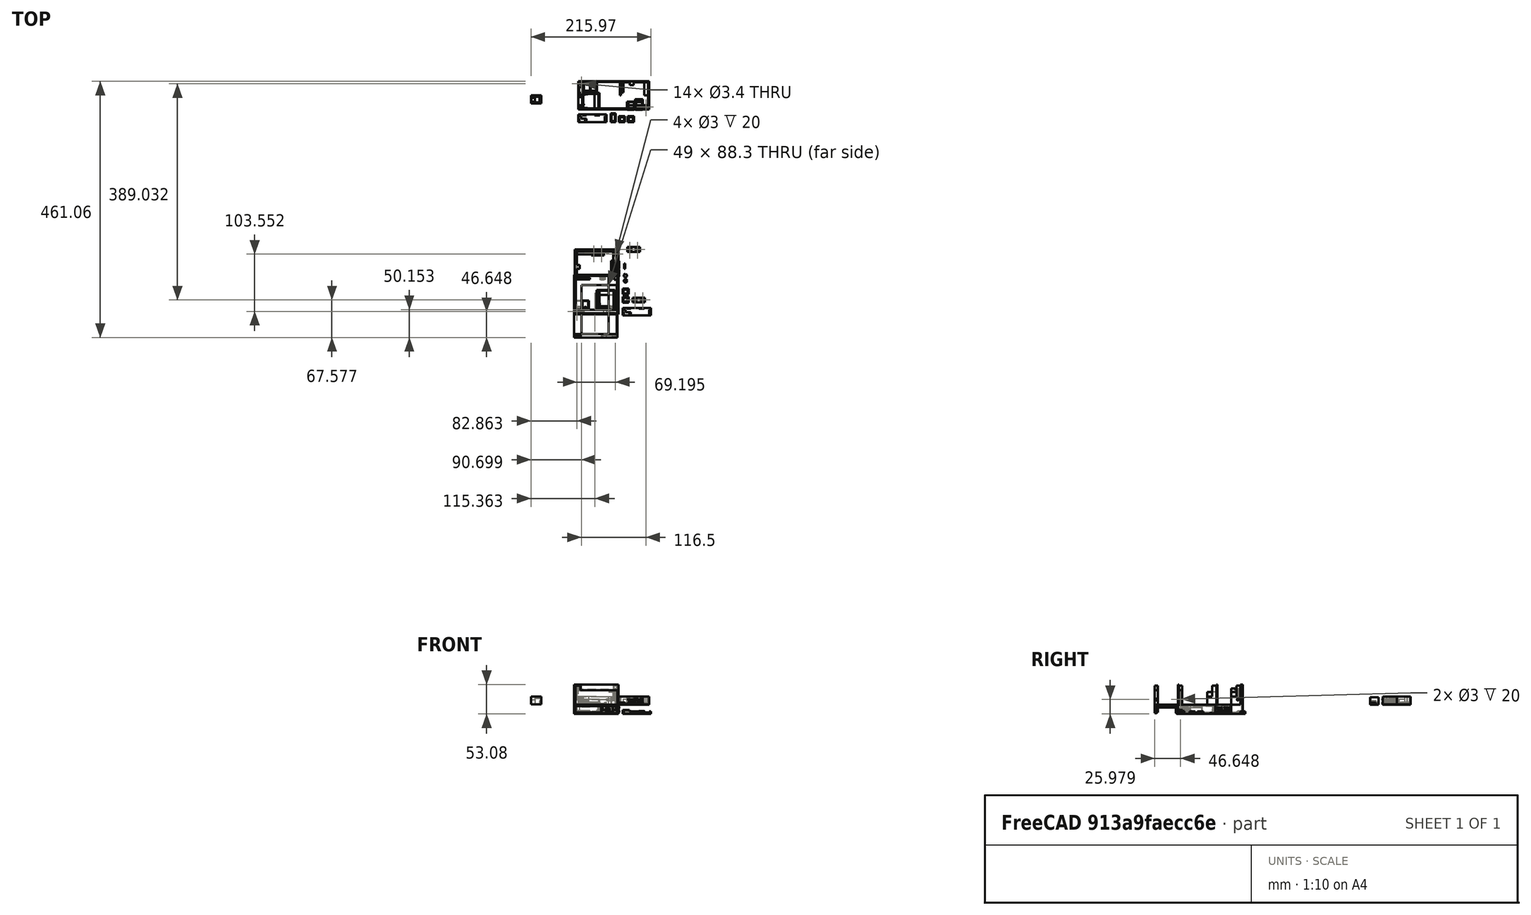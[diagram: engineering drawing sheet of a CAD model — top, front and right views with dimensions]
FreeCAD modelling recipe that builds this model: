
FCSTD DOCUMENT  (FreeCAD 0.18.4R)
Label: control.station.lamp.pump
License: All rights reserved
LicenseURL: http://en.wikipedia.org/wiki/All_rights_reserved
objects: Part::Extrusion×146, Part::Feature×99, Part::Part2DObjectPython×90, Part::MultiFuse×70, Part::Cut×57, Part::FeaturePython×25, App::DocumentObjectGroup×12, Part::Cone×5
note: 492 computed .brp shape members not serialized (recipe doc carries the construction recipe); baked Part::Feature solids carry a one-line shape summary decoded from their .brp

FEATURE [Part::Feature] Cut005001  label="Cut006"
  Placement = pos=(-97.5132,168.752,-89.7646) rot=(0,-1,0;1.57274rad)
  shape: bbox 38.06 x 11.04 x 29.87 mm, 51 faces (baked)
FEATURE [Part::Part2DObjectPython] Rectangle004  # Draft 2D object (typed FeaturePython)
  ChamferSize = 0
  Columns = 1
  FilletRadius = 0
  Height = 76.4161
  Length = 78.2176
  MakeFace = true
  Placement = pos=(-30.7742,-1.04013,-53.231) rot=(1,0,0;1.5708rad)
  Rows = 1
  Support = -> [Cut005001]
FEATURE [Part::Extrusion] Extrusion008
  Base = -> Rectangle004
  Dir = (-5.996e-12,1.04013,2.61633e-11)
  DirMode = 0
  FaceMakerClass = Part::FaceMakerBullseye
  LengthFwd = 0
  LengthRev = 0
  Solid = true
  Symmetric = false
FEATURE [Part::Cut] Cut005002
  Base = -> Cut005001
  Tool = -> Extrusion008
FEATURE [Part::Feature] Face004
  shape: bbox 0.05017 x 0.9599 x 25.8 mm, 1 faces, 0 solids (baked)
FEATURE [Part::Extrusion] Extrusion009
  Base = -> Face004
  Dir = (5.49999,-2.0138e-11,0.0106907)
  DirMode = 0
  FaceMakerClass = Part::FaceMakerBullseye
  LengthFwd = 0
  LengthRev = 0
  Solid = true
  Symmetric = false
FEATURE [Part::Cut] Cut005003
  Base = -> Cut005002
  Placement = pos=(-16.5699,14.4997,-128.121) rot=(0,1,0;0.001944rad)
  Tool = -> Extrusion009
FEATURE [Part::Feature] Face
  Placement = pos=(-35.171,9.5,-126.101) rot=(0,0,1;0rad)
  shape: bbox 15.9 x 4e-07 x 10.7 mm, 1 faces, 0 solids (baked)
FEATURE [Part::Extrusion] Extrusion016
  Base = -> Face
  Dir = (0,-1.5,0)
  DirMode = 0
  FaceMakerClass = Part::FaceMakerBullseye
  LengthFwd = 0
  LengthRev = 0
  Placement = pos=(108.58,10.9997,-148.572) rot=(0,1,0;1.5708rad)
  Solid = true
  Symmetric = false
FEATURE [Part::Feature] Face005
  Placement = pos=(-35.171,9.5,-126.101) rot=(0,0,1;0rad)
  shape: bbox 15.9 x 4e-07 x 10.7 mm, 1 faces, 0 solids (baked)
FEATURE [Part::Extrusion] Extrusion017
  Base = -> Face005
  Dir = (0,-1.5,0)
  DirMode = 0
  FaceMakerClass = Part::FaceMakerBullseye
  LengthFwd = 0
  LengthRev = 0
  Placement = pos=(-8.2,-99.2512,-120.601) rot=(1,0,0;1.5708rad)
  Solid = true
  Symmetric = false
FEATURE [Part::Feature] Fusion001002003002001  label="Fusion001002003003"
  shape: bbox 18.6 x 15 x 50.4 mm, 8 faces (baked)
FEATURE [Part::Feature] Face013
  shape: bbox 18.6 x 15 x 6.403e-07 mm, 1 faces, 0 solids (baked)
FEATURE [Part::Extrusion] Extrusion026
  Base = -> Face013
  Dir = (0,1.05e-14,-25)
  DirMode = 0
  FaceMakerClass = Part::FaceMakerBullseye
  LengthFwd = 0
  LengthRev = 0
  Solid = true
  Symmetric = false
FEATURE [Part::Cut] Cut279012005005004
  Base = -> Fusion001002003002001
  Tool = -> Extrusion026
FEATURE [Part::Part2DObjectPython] Rectangle012  # Draft 2D object (typed FeaturePython)
  ChamferSize = 0
  Columns = 1
  FilletRadius = 0
  Height = 50.4
  Length = 127.7
  MakeFace = true
  Placement = pos=(-45.471,23.4997,-158.501) rot=(1,0,0;1.5708rad)
  Rows = 1
  Support = -> [Cut005003]
FEATURE [Part::Extrusion] Extrusion028
  Base = -> Rectangle012
  Dir = (-2.8e-15,1,-1.17319e-11)
  DirMode = 0
  FaceMakerClass = Part::FaceMakerBullseye
  LengthFwd = 0
  LengthRev = 0
  Solid = true
  Symmetric = false
FEATURE [Part::Part2DObjectPython] Circle005  # Draft 2D object (typed FeaturePython)
  FirstAngle = 0
  LastAngle = 0
  MakeFace = true
  Placement = pos=(-39.871,9.5,-112.551) rot=(1,0,0;1.5708rad)
  Radius = 1.7
FEATURE [Part::Extrusion] Extrusion029
  Base = -> Circle005
  Dir = (1.7e-15,43.004,9.5e-15)
  DirMode = 0
  FaceMakerClass = Part::FaceMakerBullseye
  LengthFwd = 0
  LengthRev = 0
  Solid = true
  Symmetric = false
FEATURE [Part::Cut] Cut279012005005005
  Base = -> Extrusion028
  Tool = -> Extrusion029
FEATURE [Part::Part2DObjectPython] Circle006  # Draft 2D object (typed FeaturePython)
  FirstAngle = 0
  LastAngle = 0
  MakeFace = true
  Placement = pos=(76.629,9.5,-154.051) rot=(1,0,0;1.5708rad)
  Radius = 1.7
  Support = -> [Cut279012005005004]
FEATURE [Part::Extrusion] Extrusion030
  Base = -> Circle006
  Dir = (1e-15,47.7104,-1.06e-14)
  DirMode = 0
  FaceMakerClass = Part::FaceMakerBullseye
  LengthFwd = 0
  LengthRev = 0
  Solid = true
  Symmetric = false
FEATURE [Part::Cut] Cut279012005005006
  Base = -> Cut279012005005005
  Tool = -> Extrusion030
FEATURE [Part::Part2DObjectPython] Rectangle013  # Draft 2D object (typed FeaturePython)
  ChamferSize = 0
  Columns = 1
  FilletRadius = 0
  Height = 10.4
  Length = 8.1
  MakeFace = true
  Placement = pos=(-38.471,9.5,-130.801) rot=(1,0,0;1.5708rad)
  Rows = 1
FEATURE [Part::Part2DObjectPython] Rectangle014  # Draft 2D object (typed FeaturePython)
  ChamferSize = 0
  Columns = 1
  FilletRadius = 0
  Height = 10.4
  Length = 8.1
  MakeFace = true
  Placement = pos=(-38.471,9.5,-146.201) rot=(1,0,0;1.5708rad)
  Rows = 1
FEATURE [Part::Extrusion] Extrusion031
  Base = -> Rectangle013
  Dir = (3.6e-15,89.6542,1.99e-14)
  DirMode = 0
  FaceMakerClass = Part::FaceMakerBullseye
  LengthFwd = 0
  LengthRev = 0
  Solid = true
  Symmetric = false
FEATURE [Part::Extrusion] Extrusion032
  Base = -> Rectangle014
  Dir = (3.5e-15,84.9482,1.89e-14)
  DirMode = 0
  FaceMakerClass = Part::FaceMakerBullseye
  LengthFwd = 0
  LengthRev = 0
  Solid = true
  Symmetric = false
FEATURE [Part::Cut] Cut279012005005007
  Base = -> Cut279012005005006
  Tool = -> Extrusion032
FEATURE [Part::Cut] Cut279012005005008
  Base = -> Cut279012005005007
  Tool = -> Extrusion031
FEATURE [Part::Part2DObjectPython] Rectangle015  # Draft 2D object (typed FeaturePython)
  ChamferSize = 0
  Columns = 1
  FilletRadius = 0
  Height = 9.3
  Length = 17.1
  MakeFace = true
  Placement = pos=(-43.971,9.5,-157.001) rot=(1,0,0;1.5708rad)
  Rows = 1
FEATURE [Part::Feature] Fusion001002003002002001  label="Fusion001002003002003"
  shape: bbox 18.6 x 15 x 50.4 mm, 38 faces (baked)
FEATURE [Part::Extrusion] Extrusion033
  Base = -> Rectangle015
  Dir = (5e-16,45.0707,-1e-14)
  DirMode = 0
  FaceMakerClass = Part::FaceMakerBullseye
  LengthFwd = 0
  LengthRev = 0
  Solid = true
  Symmetric = false
FEATURE [Part::Cut] Cut279012005005009
  Base = -> Fusion001002003002002001
  Tool = -> Extrusion033
FEATURE [Part::Part2DObjectPython] Rectangle016  # Draft 2D object (typed FeaturePython)
  ChamferSize = 0
  Columns = 1
  FilletRadius = 0
  Height = 9.3
  Length = 17.1
  MakeFace = true
  Placement = pos=(-43.971,9.5,-157.001) rot=(1,0,0;1.5708rad)
  Rows = 1
  Support = -> [Cut279012005005009]
FEATURE [Part::Extrusion] Extrusion034
  Base = -> Rectangle016
  Dir = (1.8e-15,174.192,-3.87e-14)
  DirMode = 0
  FaceMakerClass = Part::FaceMakerBullseye
  LengthFwd = 0
  LengthRev = 0
  Solid = true
  Symmetric = false
FEATURE [Part::Cut] Cut279012005005010
  Base = -> Cut279012005005008
  Tool = -> Extrusion034
FEATURE [Part::Part2DObjectPython] Rectangle017  # Draft 2D object (typed FeaturePython)
  ChamferSize = 0
  Columns = 1
  FilletRadius = 0
  Height = 25.2
  Length = 9.3
  MakeFace = true
  Placement = pos=(72.929,23.4997,-133.301) rot=(1,0,0;1.5708rad)
  Rows = 1
  Support = -> [Cut279012005005010]
FEATURE [Part::Extrusion] Extrusion035
  Base = -> Rectangle017
  Dir = (-2.63e-14,9.53056,-1.11812e-10)
  DirMode = 0
  FaceMakerClass = Part::FaceMakerBullseye
  LengthFwd = 0
  LengthRev = 0
  Solid = true
  Symmetric = false
FEATURE [Part::Cut] Cut279012005005011
  Base = -> Cut279012005005010
  Tool = -> Extrusion035
FEATURE [Part::Part2DObjectPython] Rectangle018  # Draft 2D object (typed FeaturePython)
  ChamferSize = 0
  Columns = 1
  FilletRadius = 0
  Height = 16.25
  Length = 17.1
  MakeFace = true
  Placement = pos=(63.629,9.5,-150.851) rot=(1,0,0;1.5708rad)
  Rows = 1
FEATURE [Part::Extrusion] Extrusion036
  Base = -> Rectangle018
  Dir = (3e-16,13.9997,-3.1e-15)
  DirMode = 0
  FaceMakerClass = Part::FaceMakerBullseye
  LengthFwd = 0
  LengthRev = 0
  Solid = true
  Symmetric = false
FEATURE [Part::Cut] Cut279012005005012
  Base = -> Cut279012005005004
  Tool = -> Extrusion036
FEATURE [Part::Feature] Face015
  shape: bbox 6.403e-07 x 15 x 25.4 mm, 1 faces, 0 solids (baked)
FEATURE [Part::Extrusion] Extrusion037
  Base = -> Face015
  Dir = (7.3,0,-2.1e-15)
  DirMode = 0
  FaceMakerClass = Part::FaceMakerBullseye
  LengthFwd = 0
  LengthRev = 0
  Solid = true
  Symmetric = false
FEATURE [Part::Cut] Cut279012005005013
  Base = -> Cut279012005005012
  Tool = -> Extrusion037
FEATURE [Part::Feature] Fusion001002003002002003001  label="Fusion001002003002002004"
  shape: bbox 53 x 16 x 25 mm, 32 faces (baked)
FEATURE [Part::Feature] Fusion001002003002002003002  label="Fusion001002003002002005"
  shape: bbox 53 x 16 x 25 mm, 32 faces (baked)
FEATURE [Part::Part2DObjectPython] Rectangle019  # Draft 2D object (typed FeaturePython)
  ChamferSize = 0
  Columns = 1
  FilletRadius = 0
  Height = 9.44975
  Length = 9.8
  MakeFace = true
  Placement = pos=(-36.671,9.5,-118.901) rot=(1,0,0;1.5708rad)
  Rows = 1
FEATURE [Part::Extrusion] Extrusion039
  Base = -> Rectangle019
  Dir = (6e-16,13.9997,3.1e-15)
  DirMode = 0
  FaceMakerClass = Part::FaceMakerBullseye
  LengthFwd = 0
  LengthRev = 0
  Solid = true
  Symmetric = false
FEATURE [Part::Cut] Cut279012005005014
  Base = -> Cut279012005005009
  Tool = -> Extrusion039
FEATURE [Part::Part2DObjectPython] Rectangle020  # Draft 2D object (typed FeaturePython)
  ChamferSize = 0
  Columns = 1
  FilletRadius = 0
  Height = 2
  Length = 28.5
  MakeFace = true
  Placement = pos=(11.129,14.4997,-158.501) rot=(1,0,0;1.5708rad)
  Rows = 1
FEATURE [Part::Extrusion] Extrusion040
  Base = -> Rectangle020
  Dir = (-5.12376e-11,9,2.26487e-10)
  DirMode = 0
  FaceMakerClass = Part::FaceMakerBullseye
  LengthFwd = 0
  LengthRev = 0
  Solid = true
  Symmetric = false
FEATURE [Part::MultiFuse] Fusion001002003002002003003
  Shapes = -> [Cut279012005005011,Cut279012005005014,Cut005003,Fusion001002003002002003001,Extrusion040]
FEATURE [Part::Part2DObjectPython] Rectangle021  # Draft 2D object (typed FeaturePython)
  ChamferSize = 0
  Columns = 1
  FilletRadius = 0
  Height = 11.7
  Length = 16.9
  MakeFace = true
  Placement = pos=(-39.0339,9.5,-104.973) rot=(1,0,0;1.5708rad)
  Rows = 1
FEATURE [Part::Extrusion] Extrusion041
  Base = -> Rectangle021
  Dir = (-1e-16,-3,7e-16)
  DirMode = 0
  FaceMakerClass = Part::FaceMakerBullseye
  LengthFwd = 0
  LengthRev = 0
  Placement = pos=(-108.444,29.9997,-147.135) rot=(0.707107,0,-0.707107;3.14159rad)
  Solid = true
  Symmetric = false
FEATURE [Part::Part2DObjectPython] Circle007  # Draft 2D object (typed FeaturePython)
  FirstAngle = 0
  LastAngle = 0
  MakeFace = true
  Placement = pos=(-18.371,24.4997,-149.501) rot=(-1,0,0;1.5708rad)
  Radius = 1.5
  Support = -> [Fusion001002003002002003003]
FEATURE [Part::Extrusion] Extrusion042
  Base = -> Circle007
  Dir = (6.94e-14,-25.137,2.94906e-10)
  DirMode = 0
  FaceMakerClass = Part::FaceMakerBullseye
  LengthFwd = 0
  LengthRev = 0
  Solid = true
  Symmetric = false
FEATURE [Part::Cut] Cut279012005005015
  Base = -> Fusion001002003002002003003
  Tool = -> Extrusion042
FEATURE [Part::Extrusion] Extrusion043
  Base = -> Rectangle021
  Dir = (-1e-16,-3,7e-16)
  DirMode = 0
  FaceMakerClass = Part::FaceMakerBullseye
  LengthFwd = 0
  LengthRev = 0
  Placement = pos=(42.0628,116.773,-101.601) rot=(-1,0,0;1.5708rad)
  Solid = true
  Symmetric = false
FEATURE [Part::MultiFuse] Fusion001002003002002003004
  Shapes = -> [Cut279012005005015,Fusion001002003002002003002,Cut279012005005013]
FEATURE [Part::Cut] Cut279012005005016
  Base = -> Extrusion043
  Placement = pos=(-15.2708,131.601,-111.13) rot=(-0.57735,-0.57735,-0.57735;2.0944rad)
  Tool = -> Extrusion017
FEATURE [Part::Part2DObjectPython] Rectangle022  # Draft 2D object (typed FeaturePython)
  ChamferSize = 0
  Columns = 1
  FilletRadius = 0
  Height = 1
  Length = 11.7
  MakeFace = true
  Placement = pos=(8.22896,23.4997,-91.2009) rot=(0,0.707107,0.707107;3.14159rad)
  Rows = 1
FEATURE [Part::Extrusion] Extrusion044
  Base = -> Rectangle022
  Dir = (0,-3,-4e-15)
  DirMode = 0
  FaceMakerClass = Part::FaceMakerBullseye
  LengthFwd = 0
  LengthRev = 0
  Solid = true
  Symmetric = false
FEATURE [Part::MultiFuse] Fusion001002003002002003005
  Placement = pos=(-23.4,1.322e-12,-17.9) rot=(0,0,1;0rad)
  Shapes = -> [Cut279012005005016,Extrusion044]
FEATURE [Part::Feature] Face017
  Placement = pos=(-108.444,29.9997,-147.135) rot=(0.707107,0,-0.707107;3.14159rad)
  shape: bbox 11.7 x 3 x 2e-07 mm, 1 faces, 0 solids (baked)
FEATURE [Part::Extrusion] Extrusion045
  Base = -> Face017
  Dir = (-3e-16,-3e-16,-1)
  DirMode = 0
  FaceMakerClass = Part::FaceMakerBullseye
  LengthFwd = 0
  LengthRev = 0
  Solid = true
  Symmetric = false
FEATURE [Part::MultiFuse] Fusion001002003002002003006
  Shapes = -> [Extrusion041,Extrusion045]
FEATURE [Part::Feature] Face018
  shape: bbox 2e-07 x 3 x 16.9 mm, 1 faces, 0 solids (baked)
FEATURE [Part::Extrusion] Extrusion046
  Base = -> Face018
  Dir = (1,0,-3e-16)
  DirMode = 0
  FaceMakerClass = Part::FaceMakerBullseye
  LengthFwd = 0
  LengthRev = 0
  Solid = true
  Symmetric = false
FEATURE [Part::Cut] Cut279012005005017
  Base = -> Fusion001002003002002003006
  Tool = -> Extrusion016
FEATURE [Part::Feature] Face019
  shape: bbox 1 x 3 x 2e-07 mm, 1 faces, 0 solids (baked)
FEATURE [Part::Extrusion] Extrusion047
  Base = -> Face019
  Dir = (-3e-16,-3e-16,-1)
  DirMode = 0
  FaceMakerClass = Part::FaceMakerBullseye
  LengthFwd = 0
  LengthRev = 0
  Solid = true
  Symmetric = false
FEATURE [Part::MultiFuse] Fusion001002003002002003007
  Shapes = -> [Extrusion046,Extrusion047,Cut279012005005017]
FEATURE [Part::Part2DObjectPython] Circle008  # Draft 2D object (typed FeaturePython)
  FirstAngle = 0
  LastAngle = 0
  MakeFace = true
  Placement = pos=(-8.82104,20.4997,-112.101) rot=(1,0,0;1.5708rad)
  Radius = 2
  Support = -> [Fusion001002003002002003007]
FEATURE [Part::Part2DObjectPython] Circle009  # Draft 2D object (typed FeaturePython)
  FirstAngle = 0
  LastAngle = 0
  MakeFace = true
  Placement = pos=(-20.521,20.4997,-112.101) rot=(1,0,0;1.5708rad)
  Radius = 2.2
FEATURE [Part::Extrusion] Extrusion048
  Base = -> Circle008
  Dir = (-3e-16,18.8724,-8.4e-15)
  DirMode = 0
  FaceMakerClass = Part::FaceMakerBullseye
  LengthFwd = 0
  LengthRev = 0
  Solid = true
  Symmetric = false
FEATURE [Part::Extrusion] Extrusion049
  Base = -> Circle009
  Dir = (5e-16,17.7937,2.37e-14)
  DirMode = 0
  FaceMakerClass = Part::FaceMakerBullseye
  LengthFwd = 0
  LengthRev = 0
  Solid = true
  Symmetric = false
FEATURE [Part::MultiFuse] Fusion001002003002002003008
  Shapes = -> [Fusion001002003002002003004,Fusion001002003002002003007,Fusion001002003002002003005]
FEATURE [Part::Cut] Cut279012005005018
  Base = -> Fusion001002003002002003008
  Tool = -> Extrusion048
FEATURE [Part::Cut] Cut279012005005019
  Base = -> Cut279012005005018
  Tool = -> Extrusion049
FEATURE [Part::Part2DObjectPython] Rectangle023  # Draft 2D object (typed FeaturePython)
  ChamferSize = 0
  Columns = 1
  FilletRadius = 0
  Height = 83.9051
  Length = 94.4421
  MakeFace = true
  Placement = pos=(-5.29718,24.4997,-89.2462) rot=(-1,0,0;1.5708rad)
  Rows = 1
  Support = -> [Cut279012005005019]
FEATURE [Part::Extrusion] Extrusion050
  Base = -> Rectangle023
  Dir = (-2.099e-13,76.0573,-8.92301e-10)
  DirMode = 0
  FaceMakerClass = Part::FaceMakerBullseye
  LengthFwd = 0
  LengthRev = 0
  Solid = true
  Symmetric = false
FEATURE [Part::Cut] Cut279012005005020
  Base = -> Cut279012005005019
  Placement = pos=(0,183.001,-134.001) rot=(-1,0,0;1.5708rad)
  Tool = -> Extrusion050
FEATURE [Part::Part2DObjectPython] Rectangle024  # Draft 2D object (typed FeaturePython)
  ChamferSize = 0
  Columns = 1
  FilletRadius = 0
  Height = 108.906
  Length = 167.513
  MakeFace = true
  Placement = pos=(-67.949,-9.40096,-157.501) rot=(0,0,1;0rad)
  Rows = 1
  Support = -> [Cut279012005005020]
FEATURE [Part::FeaturePython] Slice  # WARN: FeaturePython — macro-defined, semantics opaque (R4)
  Base = -> Cut279012005005020
  Mode = 1
  Tolerance = 0
  Tools = -> [Rectangle024]
FEATURE [Part::FeaturePython] Slice_child0  label="Slice.0"  # WARN: FeaturePython — macro-defined, semantics opaque (R4)
  Base = -> Slice
  FilterType = 1
  Invert = false
  OverrideMaxVal = 0
  WindowFrom = 80
  WindowTo = 100
  items = 0
FEATURE [Part::FeaturePython] Slice_child1  label="Slice.1"  # WARN: FeaturePython — macro-defined, semantics opaque (R4)
  Base = -> Slice
  FilterType = 1
  Invert = false
  OverrideMaxVal = 0
  WindowFrom = 80
  WindowTo = 100
  items = 1
FEATURE [Part::FeaturePython] Slice_child2  label="Slice.2"  # WARN: FeaturePython — macro-defined, semantics opaque (R4)
  Base = -> Slice
  FilterType = 1
  Invert = false
  OverrideMaxVal = 0
  WindowFrom = 80
  WindowTo = 100
  items = 2
FEATURE [Part::Part2DObjectPython] Rectangle025  # Draft 2D object (typed FeaturePython)
  ChamferSize = 0
  Columns = 1
  FilletRadius = 0
  Height = 53.366
  Length = 63.9307
  MakeFace = true
  Placement = pos=(-26.871,20.4259,-172.171) rot=(0.57735,0.57735,0.57735;2.0944rad)
  Rows = 1
  Support = -> [Slice_child0]
FEATURE [Part::FeaturePython] Slice001  # WARN: FeaturePython — macro-defined, semantics opaque (R4)
  Base = -> Slice_child0
  Mode = 1
  Tolerance = 0
  Tools = -> [Rectangle025]
FEATURE [Part::FeaturePython] Slice001_child0  label="Slice001.0"  # WARN: FeaturePython — macro-defined, semantics opaque (R4)
  Base = -> Slice001
  FilterType = 1
  Invert = false
  OverrideMaxVal = 0
  Placement = pos=(-18.6,-1.1717e-11,5.18099e-10) rot=(0,0,1;0rad)
  WindowFrom = 80
  WindowTo = 100
  items = 0
FEATURE [Part::FeaturePython] Slice001_child2  label="Slice001.2"  # WARN: FeaturePython — macro-defined, semantics opaque (R4)
  Base = -> Slice001
  FilterType = 1
  Invert = false
  OverrideMaxVal = 0
  Placement = pos=(-9.3,8.5e-14,1.21162e-10) rot=(0,0,1;0rad)
  WindowFrom = 80
  WindowTo = 100
  items = 2
FEATURE [App::DocumentObjectGroup] GrExplode_Slice002  label="Exploded Slice002"
FEATURE [Part::FeaturePython] Slice003_child1  label="Slice003.1"  # WARN: FeaturePython — macro-defined, semantics opaque (R4)
  FilterType = 1
  Invert = false
  OverrideMaxVal = 0
  Placement = pos=(-85.1,-3.4521e-10,1.21162e-10) rot=(0,0,1;0rad)
  WindowFrom = 80
  WindowTo = 100
  items = 1
FEATURE [Part::Feature] Face020
  shape: bbox 7.019e-07 x 50.4 x 1 mm, 1 faces, 0 solids (baked)
FEATURE [Part::Extrusion] Extrusion051
  Base = -> Face020
  Dir = (85.1,2.6e-15,-2.375e-13)
  DirMode = 0
  FaceMakerClass = Part::FaceMakerBullseye
  LengthFwd = 0
  LengthRev = 0
  Solid = true
  Symmetric = false
FEATURE [Part::MultiFuse] Fusion001002003002002003009
  Shapes = -> [Slice_child1,Extrusion051]
FEATURE [Part::Part2DObjectPython] Rectangle028  # Draft 2D object (typed FeaturePython)
  ChamferSize = 0
  Columns = 1
  FilletRadius = 0
  Height = 152.897
  Length = 92.998
  MakeFace = true
  Placement = pos=(6.88981,49.8997,-45.1861) rot=(-1,0,0;1.5708rad)
  Rows = 1
FEATURE [Part::FeaturePython] Slice004  # WARN: FeaturePython — macro-defined, semantics opaque (R4)
  Base = -> Slice_child2
  Mode = 1
  Tolerance = 0
  Tools = -> [Rectangle028]
FEATURE [Part::FeaturePython] Slice004_child0  label="Slice004.0"  # WARN: FeaturePython — macro-defined, semantics opaque (R4)
  Base = -> Slice004
  FilterType = 1
  Invert = false
  OverrideMaxVal = 0
  Placement = pos=(9.3,-7e-15,-2.8e-14) rot=(0,0,1;0rad)
  WindowFrom = 80
  WindowTo = 100
  items = 0
FEATURE [Part::FeaturePython] Slice004_child1  label="Slice004.1"  # WARN: FeaturePython — macro-defined, semantics opaque (R4)
  Base = -> Slice004
  FilterType = 1
  Invert = false
  OverrideMaxVal = 0
  WindowFrom = 80
  WindowTo = 100
  items = 1
FEATURE [Part::Part2DObjectPython] Rectangle029  # Draft 2D object (typed FeaturePython)
  ChamferSize = 0
  Columns = 1
  FilletRadius = 0
  Height = 11.2
  Length = 10.6
  MakeFace = true
  Placement = pos=(-123.571,36.7997,-143.501) rot=(0,0,1;0rad)
  Rows = 1
FEATURE [Part::Extrusion] Extrusion052
  Base = -> Rectangle029
  Dir = (-1e-16,6e-16,-4)
  DirMode = 0
  FaceMakerClass = Part::FaceMakerBullseye
  LengthFwd = 0
  LengthRev = 0
  Solid = true
  Symmetric = false
FEATURE [Part::Cut] Cut279012005005021
  Base = -> Slice003_child1
  Tool = -> Extrusion052
FEATURE [Part::Feature] Face021
  Placement = pos=(-85.1,-3.4521e-10,1.21162e-10) rot=(0,0,1;0rad)
  shape: bbox 3.5 x 10.4 x 6.403e-07 mm, 1 faces, 0 solids (baked)
FEATURE [Part::Extrusion] Extrusion054
  Base = -> Face021
  Dir = (1e-16,3e-16,-1.4)
  DirMode = 0
  FaceMakerClass = Part::FaceMakerBullseye
  LengthFwd = 0
  LengthRev = 0
  Solid = true
  Symmetric = false
FEATURE [Part::Cut] Cut279012005005023
  Base = -> Cut279012005005021
  Tool = -> Extrusion054
FEATURE [Part::Feature] Face024
  shape: bbox 1 x 6.403e-07 x 1.4 mm, 1 faces, 0 solids (baked)
FEATURE [Part::Extrusion] Extrusion057
  Base = -> Face024
  Dir = (0,-8.4,-1.9e-15)
  DirMode = 0
  FaceMakerClass = Part::FaceMakerBullseye
  LengthFwd = 0
  LengthRev = 0
  Solid = true
  Symmetric = false
FEATURE [Part::MultiFuse] Fusion001002003002002003011
  Shapes = -> [Extrusion057,Cut279012005005023]
FEATURE [App::DocumentObjectGroup] GrExplode_Slice003  label="Exploded Slice003"
  Group = -> [Fusion001002003002002003011]
FEATURE [Part::Feature] Fusion001002003002002003011001  label="Fusion001002003002002003012"
  Placement = pos=(106.229,155.071,-5.99975) rot=(0,0,1;1.5708rad)
  shape: bbox 14.4 x 18.6 x 14 mm, 23 faces (baked)
FEATURE [Part::Part2DObjectPython] Circle010  # Draft 2D object (typed FeaturePython)
  FirstAngle = 0
  LastAngle = 0
  MakeFace = true
  Placement = pos=(-39.871,70.4497,-157.501) rot=(0,0,1;0rad)
  Radius = 1.7
  Support = -> [Fusion001002003002002003009]
FEATURE [Part::Extrusion] Extrusion060
  Base = -> Circle010
  Dir = (-1.949e-13,-8.19475e-10,-69.8512)
  DirMode = 0
  FaceMakerClass = Part::FaceMakerBullseye
  LengthFwd = 0
  LengthRev = 0
  Solid = true
  Symmetric = false
FEATURE [Part::Cut] Cut279012005005027
  Base = -> Fusion001002003002002003009
  Tool = -> Extrusion060
FEATURE [Part::FeaturePython] Slice005_child1  label="Slice005.1"  # WARN: FeaturePython — macro-defined, semantics opaque (R4)
  FilterType = 1
  Invert = false
  OverrideMaxVal = 0
  Placement = pos=(85.1,3.4521e-10,-1.21162e-10) rot=(0,0,1;0rad)
  WindowFrom = 80
  WindowTo = 100
  items = 1
FEATURE [Part::Part2DObjectPython] Rectangle032  # Draft 2D object (typed FeaturePython)
  ChamferSize = 0
  Columns = 1
  FilletRadius = 0
  Height = 63.2358
  Length = 40.2481
  MakeFace = true
  Placement = pos=(102.117,48.3997,-129.37) rot=(0,0.707107,-0.707107;3.14159rad)
  Rows = 1
  Support = -> [Slice004_child1]
FEATURE [Part::FeaturePython] Slice006  # WARN: FeaturePython — macro-defined, semantics opaque (R4)
  Base = -> Slice004_child1
  Mode = 1
  Tolerance = 0
  Tools = -> [Rectangle032]
FEATURE [Part::FeaturePython] Slice006_child0  label="Slice006.0"  # WARN: FeaturePython — macro-defined, semantics opaque (R4)
  Base = -> Slice006
  FilterType = 1
  Invert = false
  OverrideMaxVal = 0
  WindowFrom = 80
  WindowTo = 100
  items = 0
FEATURE [Part::Feature] Face027
  Placement = pos=(9.3,-7e-15,-2.8e-14) rot=(0,0,1;0rad)
  shape: bbox 2 x 1.136e-06 x 14 mm, 1 faces, 0 solids (baked)
FEATURE [Part::Extrusion] Extrusion061
  Base = -> Face027
  Dir = (-9.7e-14,-25.4,-1.97e-14)
  DirMode = 0
  FaceMakerClass = Part::FaceMakerBullseye
  LengthFwd = 0
  LengthRev = 0
  Solid = true
  Symmetric = false
FEATURE [Part::MultiFuse] Fusion001002003002002003011002
  Shapes = -> [Slice006_child0,Extrusion061]
FEATURE [App::DocumentObjectGroup] GrExplode_Slice006  label="Exploded Slice006"
  Group = -> [Fusion001002003002002003011002]
FEATURE [Part::Feature] Fusion001002003002002003011002001  label="Fusion001002003002002003011003"
  shape: bbox 11.3 x 25.4 x 14 mm, 10 faces (baked)
FEATURE [Part::Feature] Face028
  shape: bbox 2.036e-05 x 25 x 1 mm, 1 faces, 0 solids (baked)
FEATURE [Part::Extrusion] Extrusion062
  Base = -> Face028
  Dir = (9.3,3e-16,-2.57e-14)
  DirMode = 0
  FaceMakerClass = Part::FaceMakerBullseye
  LengthFwd = 0
  LengthRev = 0
  Solid = true
  Symmetric = false
FEATURE [Part::MultiFuse] Fusion001002003002002003011002002
  Shapes = -> [Extrusion062,Cut279012005005027]
FEATURE [Part::Feature] Cut279012005005031001  label="Cut279012005005032"
  shape: bbox 66.5 x 29.8 x 9 mm, 52 faces (baked)
FEATURE [Part::Part2DObjectPython] Circle011  # Draft 2D object (typed FeaturePython)
  FirstAngle = 0
  LastAngle = 0
  MakeFace = true
  Placement = pos=(-36.971,33.4997,-157.501) rot=(0,0,1;0rad)
  Radius = 1.5
FEATURE [Part::Extrusion] Extrusion067
  Base = -> Circle011
  Dir = (-8.66e-14,-3.63904e-10,-31.0188)
  DirMode = 0
  FaceMakerClass = Part::FaceMakerBullseye
  LengthFwd = 0
  LengthRev = 0
  Solid = true
  Symmetric = false
FEATURE [Part::Cut] Cut279012005005031002
  Base = -> Fusion001002003002002003011002002
  Tool = -> Extrusion067
FEATURE [App::DocumentObjectGroup] GrExplode_Slice  label="Exploded Slice"
  Group = -> [Slice_child0,Slice_child2,Cut279012005005031002]
FEATURE [App::DocumentObjectGroup] GrExplode_Slice007  label="Exploded Slice007"
FEATURE [Part::Part2DObjectPython] Rectangle034  # Draft 2D object (typed FeaturePython)
  ChamferSize = 0
  Columns = 1
  FilletRadius = 0
  Height = 50.5732
  Length = 65.3872
  MakeFace = true
  Placement = pos=(33.877,61.0101,-158.501) rot=(1,0,0;3.14159rad)
  Rows = 1
FEATURE [Part::FeaturePython] Slice007  # WARN: FeaturePython — macro-defined, semantics opaque (R4)
  Base = -> Fusion001002003002002003011001
  Mode = 1
  Tolerance = 0
  Tools = -> [Rectangle034]
FEATURE [Part::FeaturePython] Slice007_child0  label="Slice007.0"  # WARN: FeaturePython — macro-defined, semantics opaque (R4)
  Base = -> Slice007
  FilterType = 1
  Invert = false
  OverrideMaxVal = 0
  WindowFrom = 80
  WindowTo = 100
  items = 0
FEATURE [Part::Feature] Cut279012005005031002004
  shape: bbox 127.7 x 50.4 x 1 mm, 9 faces (baked)
FEATURE [Part::Part2DObjectPython] Rectangle035  # Draft 2D object (typed FeaturePython)
  ChamferSize = 0
  Columns = 1
  FilletRadius = 0
  Height = 8.1
  Length = 10.4
  MakeFace = true
  Placement = pos=(59.029,39.5997,-164.901) rot=(1,0,0;3.14159rad)
  Rows = 1
FEATURE [Part::Extrusion] Extrusion069
  Base = -> Rectangle035
  Dir = (-5.5814e-10,1.332e-13,47.5752)
  DirMode = 0
  FaceMakerClass = Part::FaceMakerBullseye
  LengthFwd = 0
  LengthRev = 0
  Solid = true
  Symmetric = false
FEATURE [Part::Cut] Cut279012005005031002005
  Base = -> Cut279012005005031002004
  Tool = -> Extrusion069
FEATURE [Part::Part2DObjectPython] Rectangle037  # Draft 2D object (typed FeaturePython)
  ChamferSize = 0
  Columns = 1
  FilletRadius = 0
  Height = 8.1
  Length = 10.4
  MakeFace = true
  Placement = pos=(44.629,39.5997,-158.501) rot=(1,0,0;3.14159rad)
  Rows = 1
FEATURE [Part::Extrusion] Extrusion070
  Base = -> Rectangle037
  Dir = (6.94634e-10,3.61885e-09,32.9933)
  DirMode = 0
  FaceMakerClass = Part::FaceMakerBullseye
  LengthFwd = 0
  LengthRev = 0
  Solid = true
  Symmetric = false
FEATURE [Part::Cut] Cut279012005005031002006
  Base = -> Cut279012005005031002005
  Tool = -> Extrusion070
FEATURE [Part::Feature] Face031
  Placement = pos=(106.229,155.071,-5.99975) rot=(0,0,1;1.5708rad)
  shape: bbox 3.1 x 18.6 x 2.02e-05 mm, 1 faces, 0 solids (baked)
FEATURE [Part::Extrusion] Extrusion071
  Base = -> Face031
  Dir = (7.04051e-11,7.03708e-11,5.99975)
  DirMode = 0
  FaceMakerClass = Part::FaceMakerBullseye
  LengthFwd = 0
  LengthRev = 0
  Solid = true
  Symmetric = false
FEATURE [Part::Feature] Face032
  Placement = pos=(106.229,155.071,-5.99975) rot=(0,0,1;1.5708rad)
  shape: bbox 4.1 x 18.6 x 2.02e-05 mm, 1 faces, 0 solids (baked)
FEATURE [Part::Extrusion] Extrusion072
  Base = -> Face032
  Dir = (7.04055e-11,7.03706e-11,5.99975)
  DirMode = 0
  FaceMakerClass = Part::FaceMakerBullseye
  LengthFwd = 0
  LengthRev = 0
  Solid = true
  Symmetric = false
FEATURE [Part::MultiFuse] Fusion001002003002002003011002006
  Shapes = -> [Extrusion072,Slice007_child0,Extrusion071]
FEATURE [App::DocumentObjectGroup] GrExplode_Slice007001  label="Exploded Slice008"
  Group = -> [Fusion001002003002002003011002006]
FEATURE [Part::Feature] Fusion001002003002002003011002005001  label="Fusion001002003002002003011002007"
  shape: bbox 14.4 x 18.6 x 15 mm, 23 faces (baked)
FEATURE [Part::Feature] Fusion001002003002002003011002006001  label="Fusion001002003002002003011002008"
  shape: bbox 14.4 x 18.6 x 15 mm, 23 faces (baked)
FEATURE [Part::Part2DObjectPython] Rectangle038  # Draft 2D object (typed FeaturePython)
  ChamferSize = 0
  Columns = 1
  FilletRadius = 0
  Height = 13.9997
  Length = 25
  MakeFace = true
  Placement = pos=(82.229,49.8997,-157.501) rot=(0.57735,0.57735,0.57735;2.0944rad)
  Rows = 1
  Support = -> [Slice004_child0]
FEATURE [Part::Extrusion] Extrusion073
  Base = -> Rectangle038
  Dir = (-2,0,0)
  DirMode = 0
  FaceMakerClass = Part::FaceMakerBullseye
  LengthFwd = 0
  LengthRev = 0
  Solid = true
  Symmetric = false
FEATURE [Part::MultiFuse] Fusion001002003002002003011002006002
  Shapes = -> [Slice004_child0,Extrusion073]
FEATURE [App::DocumentObjectGroup] GrExplode_Slice004  label="Exploded Slice004"
  Group = -> [Slice004_child1,Fusion001002003002002003011002006002]
FEATURE [Part::Feature] Fusion001002003002002003011002006002001  label="Fusion001002003002002003011002006003"
  shape: bbox 53 x 25 x 14 mm, 30 faces (baked)
FEATURE [Part::Feature] Face033
  Placement = pos=(85.1,3.4521e-10,-1.21162e-10) rot=(0,0,1;0rad)
  shape: bbox 4e-07 x 9.45 x 14 mm, 1 faces, 0 solids (baked)
FEATURE [Part::Extrusion] Extrusion074
  Base = -> Face033
  Dir = (0.5,0,0)
  DirMode = 0
  FaceMakerClass = Part::FaceMakerBullseye
  LengthFwd = 0
  LengthRev = 0
  Solid = true
  Symmetric = false
FEATURE [Part::MultiFuse] Fusion001002003002002003011002006002002
  Shapes = -> [Slice005_child1,Extrusion074]
FEATURE [App::DocumentObjectGroup] GrExplode_Slice005  label="Exploded Slice005"
  Group = -> [Fusion001002003002002003011002006002002]
FEATURE [Part::Feature] Fusion001002003002002003011002006002002001  label="Fusion001002003002002003011002006002003"
  shape: bbox 18.6 x 10.8 x 14 mm, 10 faces (baked)
FEATURE [Part::Cone] Cone
  Angle = 360
  AttacherType = Attacher::AttachEngine3D
  Height = 1.5
  Placement = pos=(-39.871,70.4497,-158.501) rot=(0,0,1;0rad)
  Radius1 = 3
  Radius2 = 1.7
FEATURE [Part::Cone] Cone001
  Angle = 360
  AttacherType = Attacher::AttachEngine3D
  Height = 1.5
  Placement = pos=(76.629,28.9497,-158.501) rot=(0,0,1;0rad)
  Radius1 = 3
  Radius2 = 1.7
FEATURE [Part::MultiFuse] Fusion001002003002002003011002006002002002
  Shapes = -> [Fusion001002003002002003011002001,Cut279012005005031002006]
FEATURE [Part::Cut] Cut279012005005031002007
  Base = -> Fusion001002003002002003011002006002002002
  Tool = -> Cone001
FEATURE [Part::MultiFuse] Fusion001002003002002003011002006002002003
  Shapes = -> [Fusion001002003002002003011002006002002001,Cut279012005005031002007]
FEATURE [Part::Cut] Cut279012005005031002008
  Base = -> Fusion001002003002002003011002006002002003
  Tool = -> Cone
FEATURE [Part::Feature] Face034
  shape: bbox 2.036e-05 x 1.35 x 14 mm, 1 faces, 0 solids (baked)
FEATURE [Part::Extrusion] Extrusion075
  Base = -> Face034
  Dir = (-9.3,8.93e-14,0)
  DirMode = 0
  FaceMakerClass = Part::FaceMakerBullseye
  LengthFwd = 0
  LengthRev = 0
  Solid = true
  Symmetric = false
FEATURE [Part::Cut] Cut279012005005031002009
  Base = -> Cut279012005005031002008
  Tool = -> Extrusion075
FEATURE [Part::MultiFuse] Fusion001002003002002003011002006002002004
  Shapes = -> [Fusion001002003002002003011002005001,Fusion001002003002002003011002006001,Cut279012005005031002009]
FEATURE [Part::Part2DObjectPython] Rectangle039  # Draft 2D object (typed FeaturePython)
  ChamferSize = 0
  Columns = 1
  FilletRadius = 0
  Height = 1
  Length = 23.4
  MakeFace = true
  Placement = pos=(-36.171,73.8997,-154.501) rot=(0,0,1;0rad)
  Rows = 1
  Support = -> [Slice001_child2]
FEATURE [Part::Extrusion] Extrusion076
  Base = -> Rectangle039
  Dir = (3e-16,1.2e-15,10.9997)
  DirMode = 0
  FaceMakerClass = Part::FaceMakerBullseye
  LengthFwd = 0
  LengthRev = 0
  Solid = true
  Symmetric = false
FEATURE [Part::Feature] Face035
  shape: bbox 2e-07 x 1 x 11 mm, 1 faces, 0 solids (baked)
FEATURE [Part::Extrusion] Extrusion077
  Base = -> Face035
  Dir = (1,0,0)
  DirMode = 0
  FaceMakerClass = Part::FaceMakerBullseye
  LengthFwd = 0
  LengthRev = 0
  Solid = true
  Symmetric = false
FEATURE [Part::MultiFuse] Fusion001002003002002003011002006002002005
  Shapes = -> [Extrusion076,Extrusion077]
FEATURE [Part::MultiFuse] Fusion001002003002002003011002006002002006
  Shapes = -> [Fusion001002003002002003011002006002002005,Slice001_child2]
FEATURE [Part::Feature] Face037
  Placement = pos=(-18.6,-1.1717e-11,5.18099e-10) rot=(0,0,1;0rad)
  shape: bbox 38 x 2.04e-05 x 9 mm, 1 faces, 0 solids (baked)
FEATURE [Part::Extrusion] Extrusion078
  Base = -> Face037
  Dir = (-3.52e-14,-0.35,6.1913e-12)
  DirMode = 0
  FaceMakerClass = Part::FaceMakerBullseye
  LengthFwd = 0
  LengthRev = 0
  Solid = true
  Symmetric = false
FEATURE [Part::Cut] Cut279012005005031002010
  Base = -> Cut279012005005031001
  Tool = -> Extrusion078
FEATURE [Part::Feature] Face038
  shape: bbox 66.5 x 2.041e-05 x 9 mm, 1 faces, 0 solids (baked)
FEATURE [Part::Extrusion] Extrusion079
  Base = -> Face038
  Dir = (-3.6687e-12,0.35,4.37847e-11)
  DirMode = 0
  FaceMakerClass = Part::FaceMakerBullseye
  LengthFwd = 0
  LengthRev = 0
  Solid = true
  Symmetric = false
FEATURE [Part::Cut] Cut279012005005031002011
  Base = -> Cut279012005005031002010
  Placement = pos=(3.659e-12,-0.35,-4.3798e-11) rot=(0,0,1;0rad)
  Tool = -> Extrusion079
FEATURE [Part::Part2DObjectPython] Circle012  # Draft 2D object (typed FeaturePython)
  FirstAngle = 0
  LastAngle = 0
  MakeFace = true
  Placement = pos=(-36.971,33.4997,-158.501) rot=(0,0,1;0rad)
  Radius = 1.5
  Support = -> [Fusion001002003002002003011002006002002004]
FEATURE [Part::Extrusion] Extrusion080
  Base = -> Circle012
  Dir = (5.6931e-12,-2.51654e-11,1)
  DirMode = 0
  FaceMakerClass = Part::FaceMakerBullseye
  LengthFwd = 0
  LengthRev = 0
  Solid = true
  Symmetric = false
FEATURE [Part::MultiFuse] Fusion001002003002002003011002006002002007
  Shapes = -> [Fusion001002003002002003011002006002002004,Extrusion080]
FEATURE [Part::Part2DObjectPython] Circle013  # Draft 2D object (typed FeaturePython)
  FirstAngle = 0
  LastAngle = 0
  MakeFace = true
  Placement = pos=(-36.971,33.1349,-157.501) rot=(0,0,1;0rad)
  Radius = 1.48538
  Support = -> [Fusion001002003002002003011002006002002007]
FEATURE [Part::Extrusion] Extrusion081
  Base = -> Circle013
  Dir = (-3.8499e-12,-1.10571e-09,-95.6025)
  DirMode = 0
  FaceMakerClass = Part::FaceMakerBullseye
  LengthFwd = 0
  LengthRev = 0
  Solid = true
  Symmetric = false
FEATURE [Part::Cut] Cut279012005005031002012
  Base = -> Fusion001002003002002003011002006002002007
  Tool = -> Extrusion081
FEATURE [Part::Part2DObjectPython] Rectangle040  # Draft 2D object (typed FeaturePython)
  ChamferSize = 0
  Columns = 1
  FilletRadius = 0
  Height = 13.9997
  Length = 10.5
  MakeFace = true
  Placement = pos=(-45.471,64.0997,-157.501) rot=(0.57735,-0.57735,-0.57735;2.0944rad)
  Rows = 1
  Support = -> [Cut279012005005031002012]
FEATURE [Part::Extrusion] Extrusion082
  Base = -> Rectangle040
  Dir = (1.5,1.8e-15,-9e-16)
  DirMode = 0
  FaceMakerClass = Part::FaceMakerBullseye
  LengthFwd = 0
  LengthRev = 0
  Solid = true
  Symmetric = false
FEATURE [Part::MultiFuse] Fusion001002003002002003011002006002002008
  Shapes = -> [Cut279012005005031002012,Extrusion082]
FEATURE [Part::Feature] Face039
  shape: bbox 1.5 x 2.037e-05 x 14 mm, 1 faces, 0 solids (baked)
FEATURE [Part::Extrusion] Extrusion083
  Base = -> Face039
  Dir = (1.8e-15,-1.43864,-2.2e-15)
  DirMode = 0
  FaceMakerClass = Part::FaceMakerBullseye
  LengthFwd = 0
  LengthRev = 0
  Solid = true
  Symmetric = false
FEATURE [Part::MultiFuse] Fusion001002003002002003011002006002002009
  Shapes = -> [Fusion001002003002002003011002006002002008,Extrusion083]
FEATURE [Part::Part2DObjectPython] Rectangle041  # Draft 2D object (typed FeaturePython)
  ChamferSize = 0
  Columns = 1
  FilletRadius = 0
  Height = 1.65
  Length = 66.5
  MakeFace = true
  Placement = pos=(-45.471,24.4997,-148.501) rot=(0,0,1;0rad)
  Rows = 1
  Support = -> [Cut279012005005031002011]
FEATURE [Part::Extrusion] Extrusion084
  Base = -> Rectangle041
  Dir = (2.42748e-11,-1.24412e-10,4.99975)
  DirMode = 0
  FaceMakerClass = Part::FaceMakerBullseye
  LengthFwd = 0
  LengthRev = 0
  Solid = true
  Symmetric = false
FEATURE [Part::MultiFuse] Fusion001002003002002003011002006002002010
  Shapes = -> [Cut279012005005031002011,Extrusion084]
FEATURE [Part::Part2DObjectPython] Rectangle045  # Draft 2D object (typed FeaturePython)
  ChamferSize = 0
  Columns = 1
  FilletRadius = 0
  Height = 36.542
  Length = 28.8
  MakeFace = true
  Placement = pos=(42.129,6.55773,-143.501) rot=(0,0,1;0rad)
  Rows = 1
  Support = -> [Fusion001002003002002003011002006002002009]
FEATURE [Part::Extrusion] Extrusion085
  Base = -> Rectangle045
  Dir = (-8.33388e-10,-8.33898e-10,-71.0981)
  DirMode = 0
  FaceMakerClass = Part::FaceMakerBullseye
  LengthFwd = 0
  LengthRev = 0
  Solid = true
  Symmetric = false
FEATURE [Part::Cut] Cut279012005005031002013
  Base = -> Fusion001002003002002003011002006002002009
  Tool = -> Extrusion085
FEATURE [Part::Feature] Fusion001002003002002003011002006002002011
  Placement = pos=(0,-4.5,4.25615e-10) rot=(0,0,1;0rad)
  shape: bbox 28.8 x 14.1 x 15 mm, 40 faces (baked)
FEATURE [Part::Feature] Face040
  shape: bbox 28.8 x 2.046e-05 x 1 mm, 1 faces, 0 solids (baked)
FEATURE [Part::Extrusion] Extrusion086
  Base = -> Face040
  Dir = (3.93e-14,-4.5,5.27798e-11)
  DirMode = 0
  FaceMakerClass = Part::FaceMakerBullseye
  LengthFwd = 0
  LengthRev = 0
  Solid = true
  Symmetric = false
FEATURE [Part::MultiFuse] Fusion001002003002002003011002006002002012
  Shapes = -> [Cut279012005005031002013,Extrusion086]
FEATURE [Part::MultiFuse] Fusion001002003002002003011002006002002013
  Shapes = -> [Fusion001002003002002003011002006002002012,Fusion001002003002002003011002006002002011]
FEATURE [Part::Part2DObjectPython] Circle014  # Draft 2D object (typed FeaturePython)
  FirstAngle = 0
  LastAngle = 0
  MakeFace = true
  Placement = pos=(-29.821,70.8997,-156.001) rot=(0,0,1;0rad)
  Radius = 2.2
  Support = -> [Fusion001002003002002003011002006002002006]
FEATURE [Part::Part2DObjectPython] Circle015  # Draft 2D object (typed FeaturePython)
  FirstAngle = 0
  LastAngle = 0
  MakeFace = true
  Placement = pos=(-18.121,70.8997,-156.001) rot=(0,0,1;0rad)
  Radius = 2
  Support = -> [Fusion001002003002002003011002006002002006]
FEATURE [Part::Extrusion] Extrusion101
  Base = -> Circle014
  Dir = (0,4.44e-14,-26.6491)
  DirMode = 0
  FaceMakerClass = Part::FaceMakerBullseye
  LengthFwd = 0
  LengthRev = 0
  Solid = true
  Symmetric = false
FEATURE [Part::Extrusion] Extrusion102
  Base = -> Circle015
  Dir = (0,8.7e-15,-39.0376)
  DirMode = 0
  FaceMakerClass = Part::FaceMakerBullseye
  LengthFwd = 0
  LengthRev = 0
  Solid = true
  Symmetric = false
FEATURE [Part::Cut] Cut279012005005031002016007
  Base = -> Fusion001002003002002003011002006002002013
  Tool = -> Extrusion102
FEATURE [Part::Cut] Cut279012005005031002016008
  Base = -> Cut279012005005031002016007
  Tool = -> Extrusion101
FEATURE [Part::Cone] Cone002
  Angle = 360
  AttacherType = Attacher::AttachEngine3D
  Height = 1.5
  Placement = pos=(-29.821,70.8997,-158.501) rot=(0,0,1;0rad)
  Radius1 = 3
  Radius2 = 1.7
FEATURE [Part::Cone] Cone003
  Angle = 360
  AttacherType = Attacher::AttachEngine3D
  Height = 1.5
  Placement = pos=(-18.121,70.8997,-158.501) rot=(0,0,1;0rad)
  Radius1 = 3
  Radius2 = 1.7
FEATURE [Part::Cut] Cut279012005005031002016009
  Base = -> Cut279012005005031002016008
  Tool = -> Cone003
FEATURE [Part::Cut] Cut279012005005031002016010
  Base = -> Cut279012005005031002016009
  Tool = -> Cone002
FEATURE [Part::Part2DObjectPython] Rectangle048  # Draft 2D object (typed FeaturePython)
  ChamferSize = 0
  Columns = 1
  FilletRadius = 0
  Height = 15.3
  Length = 9
  MakeFace = true
  Placement = pos=(70.929,32.1497,-143.501) rot=(0,0,1;0rad)
  Rows = 1
  Support = -> [Cut279012005005031002016010]
FEATURE [Part::Extrusion] Extrusion103
  Base = -> Rectangle048
  Dir = (0,0,-13.6)
  DirMode = 0
  FaceMakerClass = Part::FaceMakerBullseye
  LengthFwd = 0
  LengthRev = 0
  Placement = pos=(-55.5943,-36.0279,-1.39975) rot=(0,0,1;0rad)
  Solid = true
  Symmetric = false
FEATURE [Part::Part2DObjectPython] Rectangle049  # Draft 2D object (typed FeaturePython)
  ChamferSize = 0
  Columns = 1
  FilletRadius = 0
  Height = 12.3
  Length = 6
  MakeFace = true
  Placement = pos=(16.8347,-2.37819,-144.901) rot=(0,0,1;0rad)
  Rows = 1
FEATURE [Part::Extrusion] Extrusion104
  Base = -> Rectangle049
  Dir = (-9e-16,-2.8e-15,-32.4409)
  DirMode = 0
  FaceMakerClass = Part::FaceMakerBullseye
  LengthFwd = 0
  LengthRev = 0
  Solid = true
  Symmetric = false
FEATURE [Part::Cut] Cut279012005005031002016011
  Base = -> Extrusion103
  Placement = pos=(-2.38075,5.72524,2.38283e-08) rot=(0,0,1;0rad)
  Tool = -> Extrusion104
FEATURE [Part::Feature] Face046
  Placement = pos=(0,-4.5,4.25615e-10) rot=(0,0,1;0rad)
  shape: bbox 10.4 x 2.047e-05 x 1 mm, 1 faces, 0 solids (baked)
FEATURE [Part::Extrusion] Extrusion105
  Base = -> Face046
  Dir = (2.5e-15,2.5,-2.93225e-11)
  DirMode = 0
  FaceMakerClass = Part::FaceMakerBullseye
  LengthFwd = 0
  LengthRev = 0
  Solid = true
  Symmetric = false
FEATURE [Part::Feature] Face047
  Placement = pos=(0,-4.5,4.25615e-10) rot=(0,0,1;0rad)
  shape: bbox 10.4 x 2.047e-05 x 1 mm, 1 faces, 0 solids (baked)
FEATURE [Part::Extrusion] Extrusion106
  Base = -> Face047
  Dir = (2.5e-15,2.5,-2.93225e-11)
  DirMode = 0
  FaceMakerClass = Part::FaceMakerBullseye
  LengthFwd = 0
  LengthRev = 0
  Solid = true
  Symmetric = false
FEATURE [Part::Cut] Cut279012005005031002016012
  Base = -> Cut279012005005031002016010
  Tool = -> Extrusion105
FEATURE [Part::Cut] Cut279012005005031002016013
  Base = -> Cut279012005005031002016012
  Tool = -> Extrusion106
FEATURE [Part::Part2DObjectPython] Rectangle050  # Draft 2D object (typed FeaturePython)
  ChamferSize = 0
  Columns = 1
  FilletRadius = 0
  Height = 1
  Length = 10.4
  MakeFace = true
  Placement = pos=(44.629,26.9997,-157.501) rot=(-1,0,0;1.5708rad)
  Rows = 1
  Support = -> [Cut279012005005031002016013]
FEATURE [Part::Part2DObjectPython] Rectangle051  # Draft 2D object (typed FeaturePython)
  ChamferSize = 0
  Columns = 1
  FilletRadius = 0
  Height = 1
  Length = 10.4
  MakeFace = true
  Placement = pos=(59.029,26.9997,-157.501) rot=(-1,0,0;1.5708rad)
  Rows = 1
FEATURE [Part::Extrusion] Extrusion107
  Base = -> Rectangle051
  Dir = (5.1e-15,5,-5.86431e-11)
  DirMode = 0
  FaceMakerClass = Part::FaceMakerBullseye
  LengthFwd = 0
  LengthRev = 0
  Solid = true
  Symmetric = false
FEATURE [Part::Extrusion] Extrusion108
  Base = -> Rectangle050
  Dir = (5.1e-15,5,-5.86431e-11)
  DirMode = 0
  FaceMakerClass = Part::FaceMakerBullseye
  LengthFwd = 0
  LengthRev = 0
  Solid = true
  Symmetric = false
FEATURE [Part::MultiFuse] Fusion001002003002002003011002006002002014
  Shapes = -> [Cut279012005005031002016013,Extrusion107,Extrusion108]
FEATURE [Part::Feature] Cut279012005005031002016006001  label="Cut279012005005031002016014"
  shape: bbox 50.9 x 13.8 x 7 mm, 30 faces (baked)
FEATURE [Part::MultiFuse] Fusion001002003002002003011002006002002015
  Shapes = -> [Fusion001002003002002003011002006002002014,Fusion001002003002002003011002006002001,Fusion001002003002002003011002006002002006,Fusion001002003002002003011002006002002010]
FEATURE [Part::Part2DObjectPython] ShapeString002  # Draft 2D object (typed FeaturePython)
  FontFile = <path>
  Placement = pos=(59.4062,24.5,-156.769) rot=(1,0,0;1.5708rad)
  Size = 3
  String = pump
  Tracking = 0
FEATURE [Part::Extrusion] Extrude
  Base = -> ShapeString002
  Dir = (0,-1,1.17282e-11)
  DirMode = 2
  FaceMakerClass = Part::FaceMakerBullseye
  LengthFwd = 0.5
  LengthRev = 0
  Placement = pos=(0,8.669e-13,0.0738562) rot=(0,0,1;0rad)
  Solid = false
  Symmetric = false
FEATURE [Part::Part2DObjectPython] ShapeString001  # Draft 2D object (typed FeaturePython)
  FontFile = <path>
  Placement = pos=(45.0666,24.5,-156.791) rot=(1,0,0;1.5708rad)
  Size = 3
  String = lamp
  Support = -> [Fusion001002003002002003011002006002002015]
  Tracking = 0
FEATURE [Part::Extrusion] Extrude002
  Base = -> ShapeString001
  Dir = (0,-1,1.17282e-11)
  DirMode = 2
  FaceMakerClass = Part::FaceMakerBullseye
  LengthFwd = 0.5
  LengthRev = 0
  Placement = pos=(0,1.123e-12,0.0956936) rot=(0,0,1;0rad)
  Solid = false
  Symmetric = false
FEATURE [Part::Part2DObjectPython] ShapeString  # Draft 2D object (typed FeaturePython)
  FontFile = <path>
  Placement = pos=(42.5167,24.5,-149.767) rot=(1,0,0;1.5708rad)
  Size = 3
  String = +
  Tracking = 0
FEATURE [Part::Part2DObjectPython] ShapeString003  # Draft 2D object (typed FeaturePython)
  FontFile = <path>
  Placement = pos=(57.0482,24.5,-149.767) rot=(1,0,0;1.5708rad)
  Size = 3
  String = +
  Tracking = 0
FEATURE [Part::Part2DObjectPython] ShapeString004  # Draft 2D object (typed FeaturePython)
  FontFile = <path>
  Placement = pos=(53.8092,24.5,-149.604) rot=(1,0,0;1.5708rad)
  Size = 3
  String = -
  Tracking = 0
FEATURE [Part::Part2DObjectPython] ShapeString005  # Draft 2D object (typed FeaturePython)
  FontFile = <path>
  Placement = pos=(68.2184,24.5,-149.603) rot=(1,0,0;1.5708rad)
  Size = 3
  String = -
  Tracking = 0
FEATURE [Part::Extrusion] Extrude003
  Base = -> ShapeString
  Dir = (-3e-16,-1,1.17282e-11)
  DirMode = 2
  FaceMakerClass = Part::FaceMakerBullseye
  LengthFwd = 0.5
  LengthRev = 0
  Solid = false
  Symmetric = false
FEATURE [Part::Extrusion] Extrude004
  Base = -> ShapeString
  Dir = (-3e-16,-1,1.17282e-11)
  DirMode = 2
  FaceMakerClass = Part::FaceMakerBullseye
  LengthFwd = 0.5
  LengthRev = 0
  Solid = false
  Symmetric = false
FEATURE [Part::Extrusion] Extrude005
  Base = -> ShapeString004
  Dir = (0,-1,1.17282e-11)
  DirMode = 2
  FaceMakerClass = Part::FaceMakerBullseye
  LengthFwd = 0.5
  LengthRev = 0
  Solid = false
  Symmetric = false
FEATURE [Part::Extrusion] Extrude007
  Base = -> ShapeString003
  Dir = (0,-1,1.17282e-11)
  DirMode = 2
  FaceMakerClass = Part::FaceMakerBullseye
  LengthFwd = 0.5
  LengthRev = 0
  Solid = false
  Symmetric = false
FEATURE [Part::Extrusion] Extrude008
  Base = -> ShapeString003
  Dir = (0,-1,1.17282e-11)
  DirMode = 2
  FaceMakerClass = Part::FaceMakerBullseye
  LengthFwd = 0.5
  LengthRev = 0
  Solid = false
  Symmetric = false
FEATURE [Part::Extrusion] Extrude009
  Base = -> ShapeString005
  Dir = (0,-1,1.17282e-11)
  DirMode = 2
  FaceMakerClass = Part::FaceMakerBullseye
  LengthFwd = 0.5
  LengthRev = 0
  Solid = false
  Symmetric = false
FEATURE [Part::Extrusion] Extrude010
  Base = -> ShapeString005
  Dir = (0,-1,1.17282e-11)
  DirMode = 2
  FaceMakerClass = Part::FaceMakerBullseye
  LengthFwd = 0.5
  LengthRev = 0
  Solid = false
  Symmetric = false
FEATURE [Part::MultiFuse] Fusion001002003002002003011002006002002016
  Shapes = -> [Extrude,Extrude002,Extrude004,Extrude005,Extrude008,Extrude010,Extrude009,Extrude007,Extrude003]
FEATURE [Part::MultiFuse] Fusion001002003002002003011002006002002017
  Shapes = -> [Fusion001002003002002003011002006002002016,Fusion001002003002002003011002006002002015]
FEATURE [Part::Part2DObjectPython] Rectangle  # Draft 2D object (typed FeaturePython)
  ChamferSize = 0
  Columns = 1
  FilletRadius = 0
  Height = 13.9997
  Length = 1.65
  MakeFace = true
  Placement = pos=(21.029,24.4997,-157.501) rot=(0.57735,0.57735,0.57735;2.0944rad)
  Rows = 1
  Support = -> [Fusion001002003002002003011002006002002017]
FEATURE [Part::Extrusion] Extrusion
  Base = -> Rectangle
  Dir = (21.1,-1.87106e-10,-3.0723e-10)
  DirMode = 0
  FaceMakerClass = Part::FaceMakerBullseye
  LengthFwd = 0
  LengthRev = 0
  Solid = true
  Symmetric = false
FEATURE [Part::MultiFuse] Fusion
  Shapes = -> [Extrusion,Fusion001002003002002003011002006002002017]
FEATURE [Part::Feature] Face048
  shape: bbox 10.4 x 5 x 2.047e-05 mm, 1 faces, 0 solids (baked)
FEATURE [Part::Extrusion] Extrusion109
  Base = -> Face048
  Dir = (1e-16,2.34572e-11,2)
  DirMode = 0
  FaceMakerClass = Part::FaceMakerBullseye
  LengthFwd = 0
  LengthRev = 0
  Solid = true
  Symmetric = false
FEATURE [Part::Feature] Face049
  shape: bbox 10.4 x 5 x 2.037e-05 mm, 1 faces, 0 solids (baked)
FEATURE [Part::Extrusion] Extrusion110
  Base = -> Face049
  Dir = (1e-16,2.34572e-11,2)
  DirMode = 0
  FaceMakerClass = Part::FaceMakerBullseye
  LengthFwd = 0
  LengthRev = 0
  Solid = true
  Symmetric = false
FEATURE [Part::Feature] Face050
  Placement = pos=(106.229,150.571,-5.99975) rot=(0,0,1;1.5708rad)
  shape: bbox 0.8 x 10.6 x 2.047e-05 mm, 1 faces, 0 solids (baked)
FEATURE [Part::Extrusion] Extrusion111
  Base = -> Face050
  Dir = (2.347e-11,2.3458e-11,2)
  DirMode = 0
  FaceMakerClass = Part::FaceMakerBullseye
  LengthFwd = 0
  LengthRev = 0
  Solid = true
  Symmetric = false
FEATURE [Part::Feature] Face051
  Placement = pos=(91.8287,150.571,-5.99975) rot=(0,0,1;1.5708rad)
  shape: bbox 0.8 x 10.6 x 2.037e-05 mm, 1 faces, 0 solids (baked)
FEATURE [Part::Extrusion] Extrusion112
  Base = -> Face051
  Dir = (2.347e-11,2.3458e-11,2)
  DirMode = 0
  FaceMakerClass = Part::FaceMakerBullseye
  LengthFwd = 0
  LengthRev = 0
  Solid = true
  Symmetric = false
FEATURE [Part::MultiFuse] Fusion001002003002002003011002006002002018
  Shapes = -> [Extrusion109,Extrusion110,Extrusion112,Extrusion111]
FEATURE [Part::MultiFuse] Fusion001002003002002003011002006002002019
  Shapes = -> [Fusion001002003002002003011002006002002018,Fusion]
FEATURE [Part::Feature] Cut279012005005031002016006002  label="Cut279012005005031002016015"
  Placement = pos=(0,-25.1527,-10.6997) rot=(0,0,1;0rad)
  shape: bbox 10.9 x 10.3 x 4.3 mm, 10 faces (baked)
FEATURE [Part::Feature] Cut279012005005031002016006003  label="Cut279012005005031002016016"
  Placement = pos=(-15.9786,-25.1527,-10.6997) rot=(0,0,1;0rad)
  shape: bbox 10.9 x 10.3 x 4.3 mm, 10 faces (baked)
FEATURE [Part::Feature] Face052
  shape: bbox 1 x 15.9 x 2e-07 mm, 1 faces, 0 solids (baked)
FEATURE [Part::Extrusion] Extrusion113
  Base = -> Face052
  Dir = (0,2e-16,0.5)
  DirMode = 0
  FaceMakerClass = Part::FaceMakerBullseye
  LengthFwd = 0
  LengthRev = 0
  Solid = true
  Symmetric = false
FEATURE [Part::Feature] Face053
  shape: bbox 11.7 x 16.9 x 1.136e-06 mm, 1 faces, 0 solids (baked)
FEATURE [Part::Extrusion] Extrusion114
  Base = -> Face053
  Dir = (0,-5e-16,0.5)
  DirMode = 0
  FaceMakerClass = Part::FaceMakerBullseye
  LengthFwd = 0
  LengthRev = 0
  Solid = true
  Symmetric = false
FEATURE [Part::Feature] Face054
  Placement = pos=(-9.3,183.001,-134.001) rot=(-1,0,0;1.5708rad)
  shape: bbox 11.7 x 1 x 4e-07 mm, 1 faces, 0 solids (baked)
FEATURE [Part::Extrusion] Extrusion115
  Base = -> Face054
  Dir = (0,1e-16,0.5)
  DirMode = 0
  FaceMakerClass = Part::FaceMakerBullseye
  LengthFwd = 0
  LengthRev = 0
  Solid = true
  Symmetric = false
FEATURE [Part::Feature] Face055
  Placement = pos=(-9.3,183.001,-134.001) rot=(-1,0,0;1.5708rad)
  shape: bbox 1 x 1 x 2e-07 mm, 1 faces, 0 solids (baked)
FEATURE [Part::Extrusion] Extrusion116
  Base = -> Face055
  Dir = (0,1e-16,0.5)
  DirMode = 0
  FaceMakerClass = Part::FaceMakerBullseye
  LengthFwd = 0
  LengthRev = 0
  Solid = true
  Symmetric = false
FEATURE [Part::Feature] Face056
  shape: bbox 1 x 15.9 x 4e-07 mm, 1 faces, 0 solids (baked)
FEATURE [Part::Extrusion] Extrusion117
  Base = -> Face056
  Dir = (0,0,0.5)
  DirMode = 0
  FaceMakerClass = Part::FaceMakerBullseye
  LengthFwd = 0
  LengthRev = 0
  Solid = true
  Symmetric = false
FEATURE [Part::MultiFuse] Fusion001002003002002003011002006002002020
  Shapes = -> [Extrusion114,Extrusion117,Extrusion115,Extrusion113,Extrusion116]
FEATURE [Part::MultiFuse] Fusion001002003002002003011002006002002021
  Shapes = -> [Fusion001002003002002003011002006002002019,Fusion001002003002002003011002006002002020]
FEATURE [Part::Part2DObjectPython] Rectangle056  # Draft 2D object (typed FeaturePython)
  ChamferSize = 0
  Columns = 1
  FilletRadius = 0
  Height = 1
  Length = 7.2
  MakeFace = true
  Placement = pos=(46.229,24.4997,-143.501) rot=(0,0,1;0rad)
  Rows = 1
  Support = -> [Fusion001002003002002003011002006002002021]
FEATURE [Part::Extrusion] Extrusion118
  Base = -> Rectangle056
  Dir = (-5.8677e-11,-5.86679e-11,-5)
  DirMode = 0
  FaceMakerClass = Part::FaceMakerBullseye
  LengthFwd = 0
  LengthRev = 0
  Solid = true
  Symmetric = false
FEATURE [Part::Feature] Extrusion119
  Placement = pos=(14.3773,9.912e-13,0.0827474) rot=(0,0,1;0rad)
  shape: bbox 7.2 x 1 x 5 mm, 6 faces (baked)
FEATURE [Part::MultiFuse] Fusion001002003002002003011002006002002022
  Shapes = -> [Fusion001002003002002003011002006002002021,Extrusion118,Extrusion119]
FEATURE [Part::Part2DObjectPython] Rectangle057  # Draft 2D object (typed FeaturePython)
  ChamferSize = 0
  Columns = 1
  FilletRadius = 0
  Height = 13.9997
  Length = 1
  MakeFace = true
  Placement = pos=(-11.771,73.8997,-157.501) rot=(0.57735,0.57735,0.57735;2.0944rad)
  Rows = 1
FEATURE [Part::Extrusion] Extrusion120
  Base = -> Rectangle057
  Dir = (41,0,0)
  DirMode = 0
  FaceMakerClass = Part::FaceMakerBullseye
  LengthFwd = 0
  LengthRev = 0
  Solid = true
  Symmetric = false
FEATURE [Part::MultiFuse] Fusion001002003002002003011002006002002023
  Shapes = -> [Extrusion120,Fusion001002003002002003011002006002002022]
FEATURE [App::DocumentObjectGroup] GrExplode_Slice001  label="Exploded Slice001"
  Group = -> [Slice001_child0,Fusion001002003002002003011002006002002023]
FEATURE [Part::Feature] Face057
  shape: bbox 5.176e-05 x 27.66 x 9 mm, 1 faces, 0 solids (baked)
FEATURE [Part::Feature] Face058
  Placement = pos=(-18.6,-0.35,4.74301e-10) rot=(0,0,1;0rad)
  shape: bbox 2 x 5.176e-05 x 1.9 mm, 1 faces, 0 solids (baked)
FEATURE [Part::Part2DObjectPython] Rectangle059  # Draft 2D object (typed FeaturePython)
  ChamferSize = 0
  Columns = 1
  FilletRadius = 0
  Height = 8
  Length = 8
  MakeFace = true
  Placement = pos=(19.2926,-275.157,-158.501) rot=(1,0,0;3.14159rad)
  Rows = 1
FEATURE [Part::Extrusion] Extrusion121
  Base = -> Rectangle059
  Dir = (0,0,34.6)
  DirMode = 0
  FaceMakerClass = Part::FaceMakerBullseye
  LengthFwd = 0
  LengthRev = 0
  Solid = true
  Symmetric = false
FEATURE [Part::Feature] Face059
  shape: bbox 2e-07 x 8 x 34.6 mm, 1 faces, 0 solids (baked)
FEATURE [Part::Extrusion] Extrusion122
  Base = -> Face059
  Dir = (-2,1e-16,0)
  DirMode = 0
  FaceMakerClass = Part::FaceMakerBullseye
  LengthFwd = 0
  LengthRev = 0
  Solid = true
  Symmetric = false
FEATURE [Part::Cut] Cut
  Base = -> Extrusion121
  Tool = -> Extrusion122
FEATURE [Part::Part2DObjectPython] Rectangle060  # Draft 2D object (typed FeaturePython)
  ChamferSize = 0
  Columns = 1
  FilletRadius = 0
  Height = 6
  Length = 76
  MakeFace = true
  Placement = pos=(-50.7074,-380.157,-158.501) rot=(1,0,0;3.14159rad)
  Rows = 1
FEATURE [Part::Extrusion] Extrusion123
  Base = -> Rectangle060
  Dir = (0,0,26)
  DirMode = 0
  FaceMakerClass = Part::FaceMakerBullseye
  LengthFwd = 0
  LengthRev = 0
  Solid = true
  Symmetric = false
FEATURE [Part::Part2DObjectPython] Rectangle061  # Draft 2D object (typed FeaturePython)
  ChamferSize = 0
  Columns = 1
  FilletRadius = 0
  Height = 17.5
  Length = 16
  MakeFace = true
  Placement = pos=(9.29264,-275.157,-158.501) rot=(1,0,0;3.14159rad)
  Rows = 1
FEATURE [Part::Extrusion] Extrusion124
  Base = -> Rectangle061
  Dir = (0,0,23)
  DirMode = 0
  FaceMakerClass = Part::FaceMakerBullseye
  LengthFwd = 0
  LengthRev = 0
  Solid = true
  Symmetric = false
FEATURE [Part::Feature] Face060
  shape: bbox 2e-07 x 17.5 x 23 mm, 1 faces, 0 solids (baked)
FEATURE [Part::Feature] Face061
  shape: bbox 2e-07 x 17.5 x 23 mm, 1 faces, 0 solids (baked)
FEATURE [Part::Feature] Face063
  shape: bbox 2e-07 x 17.5 x 23 mm, 1 faces, 0 solids (baked)
FEATURE [Part::Part2DObjectPython] Rectangle062  # Draft 2D object (typed FeaturePython)
  ChamferSize = 0
  Columns = 1
  FilletRadius = 0
  Height = 8
  Length = 9.5
  MakeFace = true
  Placement = pos=(25.2926,-292.657,-143.501) rot=(0.57735,0.57735,0.57735;2.0944rad)
  Rows = 1
FEATURE [Part::Feature] Face064
  shape: bbox 2e-07 x 17.5 x 23 mm, 1 faces, 0 solids (baked)
FEATURE [Part::Extrusion] Extrusion125
  Base = -> Rectangle062
  Dir = (-1,5.48417e-11,5.48418e-11)
  DirMode = 0
  FaceMakerClass = Part::FaceMakerBullseye
  LengthFwd = 0
  LengthRev = 0
  Solid = true
  Symmetric = false
FEATURE [Part::Cut] Cut279012005005031002016006004
  Base = -> Extrusion124
  Tool = -> Extrusion125
FEATURE [Part::Part2DObjectPython] Rectangle063  # Draft 2D object (typed FeaturePython)
  ChamferSize = 0
  Columns = 1
  FilletRadius = 0
  Height = 36.6
  Length = 111
  MakeFace = true
  Placement = pos=(-50.7074,-275.157,-158.501) rot=(0.57735,-0.57735,-0.57735;2.0944rad)
  Rows = 1
  Support = -> [Extrusion123]
FEATURE [Part::Part2DObjectPython] Rectangle064  # Draft 2D object (typed FeaturePython)
  ChamferSize = 0
  Columns = 1
  FilletRadius = 0
  Height = 10
  Length = 6
  MakeFace = true
  Placement = pos=(-50.7074,-380.157,-132.501) rot=(0,0,-1;1.5708rad)
  Rows = 1
FEATURE [Part::Extrusion] Extrusion127
  Base = -> Rectangle064
  Dir = (1.81064e-10,9.43285e-10,8.6)
  DirMode = 0
  FaceMakerClass = Part::FaceMakerBullseye
  LengthFwd = 0
  LengthRev = 0
  Solid = true
  Symmetric = false
FEATURE [Part::MultiFuse] Fusion001002003002002003011002006002002024
  Placement = pos=(0,0.8,0) rot=(0,0,1;0rad)
  Shapes = -> [Cut,Cut279012005005031002016006004]
FEATURE [Part::Part2DObjectPython] Rectangle065  # Draft 2D object (typed FeaturePython)
  ChamferSize = 0
  Columns = 1
  FilletRadius = 0
  Height = 111.8
  Length = 78
  MakeFace = true
  Placement = pos=(-52.7074,-274.357,-158.501) rot=(1,0,0;3.14159rad)
  Rows = 1
  Support = -> [Extrusion123]
FEATURE [Part::Part2DObjectPython] Circle  # Draft 2D object (typed FeaturePython)
  FirstAngle = 0
  LastAngle = 0
  MakeFace = true
  Placement = pos=(-46.7074,-382.157,-123.901) rot=(0,0,-1;1.5708rad)
  Radius = 1.6
FEATURE [Part::Extrusion] Extrusion129
  Base = -> Circle
  Dir = (-1.81068e-10,-9.43287e-10,-8.6)
  DirMode = 0
  FaceMakerClass = Part::FaceMakerBullseye
  LengthFwd = 0
  LengthRev = 0
  Solid = true
  Symmetric = false
FEATURE [Part::Cut] Cut279012005005031002016006006
  Base = -> Extrusion127
  Tool = -> Extrusion129
FEATURE [Part::Part2DObjectPython] Circle017  # Draft 2D object (typed FeaturePython)
  FirstAngle = 0
  LastAngle = 0
  MakeFace = true
  Placement = pos=(-46.7074,-382.157,-123.901) rot=(0,0,1;0rad)
  Radius = 1.6
  Support = -> [Cut279012005005031002016006006]
FEATURE [Part::Extrusion] Extrusion131
  Base = -> Circle017
  Dir = (-1.81064e-10,-9.43285e-10,-8.6)
  DirMode = 0
  FaceMakerClass = Part::FaceMakerBullseye
  LengthFwd = 0
  LengthRev = 0
  Solid = true
  Symmetric = false
FEATURE [Part::MultiFuse] Fusion001002003002002003011002006002002024002
  Shapes = -> [Cut279012005005031002016006006,Extrusion131]
FEATURE [Part::Part2DObjectPython] Circle018  # Draft 2D object (typed FeaturePython)
  FirstAngle = 0
  LastAngle = 0
  MakeFace = true
  Placement = pos=(-46.7074,-383.157,-123.901) rot=(0,0,1;0rad)
  Radius = 1.5
  Support = -> [Fusion001002003002002003011002006002002024002]
FEATURE [Part::Extrusion] Extrusion132
  Base = -> Circle018
  Dir = (-1.81064e-10,-9.43285e-10,-8.6)
  DirMode = 0
  FaceMakerClass = Part::FaceMakerBullseye
  LengthFwd = 0
  LengthRev = 0
  Solid = true
  Symmetric = false
FEATURE [Part::Cut] Cut279012005005031002016006008
  Base = -> Fusion001002003002002003011002006002002024002
  Tool = -> Extrusion132
FEATURE [Part::MultiFuse] Fusion001002003002002003011002006002002024003
  Shapes = -> [Extrusion123,Cut279012005005031002016006008]
FEATURE [Part::Feature] Fusion001002003002002003011002006002002024003001  label="Fusion001002003002002003011002006002002024004"
  shape: bbox 76 x 6 x 34.6 mm, 10 faces (baked)
FEATURE [Part::Part2DObjectPython] Circle019  # Draft 2D object (typed FeaturePython)
  FirstAngle = 0
  LastAngle = 0
  MakeFace = true
  Placement = pos=(25.2926,-383.157,-149.001) rot=(0.57735,0.57735,0.57735;2.0944rad)
  Radius = 1.5
FEATURE [Part::Extrusion] Extrusion133
  Base = -> Circle019
  Dir = (-10,0,0)
  DirMode = 0
  FaceMakerClass = Part::FaceMakerBullseye
  LengthFwd = 0
  LengthRev = 0
  Solid = true
  Symmetric = false
FEATURE [Part::Cut] Cut279012005005031002016006009
  Base = -> Fusion001002003002002003011002006002002024003001
  Tool = -> Extrusion133
FEATURE [Part::Extrusion] Extrusion135
  Base = -> Rectangle065
  Dir = (-4.21076e-11,-2.19369e-10,-2)
  DirMode = 0
  FaceMakerClass = Part::FaceMakerBullseye
  LengthFwd = 0
  LengthRev = 0
  Solid = true
  Symmetric = false
FEATURE [Part::Feature] Face066
  shape: bbox 78 x 2.002e-07 x 2 mm, 1 faces, 0 solids (baked)
FEATURE [Part::Extrusion] Extrusion136
  Base = -> Face066
  Dir = (0,-0.8,8.77474e-11)
  DirMode = 0
  FaceMakerClass = Part::FaceMakerBullseye
  LengthFwd = 0
  LengthRev = 0
  Solid = true
  Symmetric = false
FEATURE [Part::Cut] Cut279012005005031002016006011
  Base = -> Extrusion135
  Tool = -> Extrusion136
FEATURE [Part::Part2DObjectPython] Rectangle068  # Draft 2D object (typed FeaturePython)
  ChamferSize = 0
  Columns = 1
  FilletRadius = 0
  Height = 36.6
  Length = 78
  MakeFace = true
  Placement = pos=(25.2926,-275.157,-160.501) rot=(0,0.707107,0.707107;3.14159rad)
  Rows = 1
FEATURE [Part::Extrusion] Extrusion139
  Base = -> Rectangle068
  Dir = (-1.7e-15,2,-2.19366e-10)
  DirMode = 0
  FaceMakerClass = Part::FaceMakerBullseye
  LengthFwd = 0
  LengthRev = 0
  Solid = true
  Symmetric = false
FEATURE [Part::Feature] Face067
  shape: bbox 78 x 2 x 2.019e-07 mm, 1 faces, 0 solids (baked)
FEATURE [Part::Extrusion] Extrusion140
  Base = -> Face067
  Dir = (4.21085e-11,2.19366e-10,2)
  DirMode = 0
  FaceMakerClass = Part::FaceMakerBullseye
  LengthFwd = 0
  LengthRev = 0
  Solid = true
  Symmetric = false
FEATURE [Part::MultiFuse] Fusion001002003002002003011002006002002024003002
  Shapes = -> [Extrusion139,Extrusion140]
FEATURE [Part::Part2DObjectPython] Rectangle069  # Draft 2D object (typed FeaturePython)
  ChamferSize = 0
  Columns = 1
  FilletRadius = 0
  Height = 49
  Length = 88.3
  MakeFace = true
  Placement = pos=(9.29264,-380.157,-158.501) rot=(0,0,1;1.5708rad)
  Rows = 1
FEATURE [Part::Extrusion] Extrusion142
  Base = -> Rectangle069
  Dir = (-8.2588e-10,-4.30257e-09,-39.2268)
  DirMode = 0
  FaceMakerClass = Part::FaceMakerBullseye
  LengthFwd = 0
  LengthRev = 0
  Solid = true
  Symmetric = false
FEATURE [Part::Cut] Cut279012005005031002016006014
  Base = -> Cut279012005005031002016006011
  Tool = -> Extrusion142
FEATURE [Part::Feature] Face069
  shape: bbox 49 x 3.002e-07 x 2 mm, 1 faces, 0 solids (baked)
FEATURE [Part::Part2DObjectPython] Rectangle070  # Draft 2D object (typed FeaturePython)
  ChamferSize = 0
  Columns = 1
  FilletRadius = 0
  Height = 38
  Length = 1.5
  MakeFace = true
  Placement = pos=(23.7926,-386.157,-163.501) rot=(0,0,1;0rad)
  Rows = 1
FEATURE [Part::Extrusion] Extrusion146
  Base = -> Rectangle070
  Dir = (-3.22823e-10,6.64324e-10,4.99975)
  DirMode = 0
  FaceMakerClass = Part::FaceMakerBullseye
  LengthFwd = 0
  LengthRev = 0
  Solid = true
  Symmetric = false
FEATURE [Part::Part2DObjectPython] Rectangle071  # Draft 2D object (typed FeaturePython)
  ChamferSize = 0
  Columns = 1
  FilletRadius = 0
  Height = 14.9997
  Length = 1.5
  MakeFace = true
  Placement = pos=(23.7926,-348.157,-158.501) rot=(-1,0,0;1.5708rad)
  Rows = 1
FEATURE [Part::Extrusion] Extrusion147
  Base = -> Rectangle071
  Dir = (-5.49319e-11,75,-9.38941e-09)
  DirMode = 0
  FaceMakerClass = Part::FaceMakerBullseye
  LengthFwd = 0
  LengthRev = 0
  Solid = true
  Symmetric = false
FEATURE [Part::Feature] Face075
  Placement = pos=(50.1424,-355.286,-14.9997) rot=(0,0,1;1.5708rad)
  shape: bbox 6.15 x 2 x 5.181e-05 mm, 1 faces, 0 solids (baked)
FEATURE [Part::Feature] Face078
  Placement = pos=(50.1424,-355.286,-14.9997) rot=(0,0,1;1.5708rad)
  shape: bbox 6.15 x 2 x 5.181e-05 mm, 1 faces, 0 solids (baked)
FEATURE [Part::Extrusion] Extrusion150
  Base = -> Face078
  Dir = (7.82622e-09,1.04357e-09,9.25962)
  DirMode = 0
  FaceMakerClass = Part::FaceMakerBullseye
  LengthFwd = 0
  LengthRev = 0
  Solid = true
  Symmetric = false
FEATURE [Part::Feature] Face079
  Placement = pos=(50.1424,-355.286,-14.9997) rot=(0,0,1;1.5708rad)
  shape: bbox 6.15 x 2 x 5.18e-05 mm, 1 faces, 0 solids (baked)
FEATURE [Part::Extrusion] Extrusion151
  Base = -> Face079
  Dir = (7.82622e-09,1.04357e-09,9.25962)
  DirMode = 0
  FaceMakerClass = Part::FaceMakerBullseye
  LengthFwd = 0
  LengthRev = 0
  Solid = true
  Symmetric = false
FEATURE [Part::Feature] Face080
  Placement = pos=(49.7924,-336.686,-14.9997) rot=(0,0,1;1.5708rad)
  shape: bbox 29.1 x 5.186e-05 x 10 mm, 1 faces, 0 solids (baked)
FEATURE [Part::Extrusion] Extrusion152
  Base = -> Face080
  Dir = (-7.0372e-12,-4,4.96926e-10)
  DirMode = 0
  FaceMakerClass = Part::FaceMakerBullseye
  LengthFwd = 0
  LengthRev = 0
  Solid = true
  Symmetric = false
FEATURE [Part::Feature] Face081
  shape: bbox 6.15 x 5.176e-05 x 9.26 mm, 1 faces, 0 solids (baked)
FEATURE [Part::Extrusion] Extrusion153
  Base = -> Face081
  Dir = (1.729e-13,-4,4.50807e-10)
  DirMode = 0
  FaceMakerClass = Part::FaceMakerBullseye
  LengthFwd = 0
  LengthRev = 0
  Solid = true
  Symmetric = false
FEATURE [Part::Feature] Face082
  shape: bbox 6.15 x 5.176e-05 x 9.26 mm, 1 faces, 0 solids (baked)
FEATURE [Part::Extrusion] Extrusion154
  Base = -> Face082
  Dir = (1.729e-13,-4,4.50807e-10)
  DirMode = 0
  FaceMakerClass = Part::FaceMakerBullseye
  LengthFwd = 0
  LengthRev = 0
  Solid = true
  Symmetric = false
FEATURE [Part::Feature] Face083
  shape: bbox 1.439 x 4 x 5.186e-05 mm, 1 faces, 0 solids (baked)
FEATURE [Part::Extrusion] Extrusion155
  Base = -> Face083
  Dir = (-3.17381e-10,6.21126e-10,4.99975)
  DirMode = 0
  FaceMakerClass = Part::FaceMakerBullseye
  LengthFwd = 0
  LengthRev = 0
  Solid = true
  Symmetric = false
FEATURE [Part::Part2DObjectPython] Rectangle073  # Draft 2D object (typed FeaturePython)
  ChamferSize = 0
  Columns = 1
  FilletRadius = 0
  Height = 6
  Length = 46.9
  MakeFace = true
  Placement = pos=(-50.7074,-380.157,-158.501) rot=(1,0,0;3.14159rad)
  Rows = 1
  Support = -> [Cut279012005005031002016006009]
FEATURE [Part::Extrusion] Extrusion156
  Base = -> Rectangle073
  Dir = (-2.94748e-10,-1.53555e-09,-13.9997)
  DirMode = 0
  FaceMakerClass = Part::FaceMakerBullseye
  LengthFwd = 0
  LengthRev = 0
  Solid = true
  Symmetric = false
FEATURE [Part::Feature] Face084
  shape: bbox 1.439 x 5.186e-05 x 5 mm, 1 faces, 0 solids (baked)
FEATURE [Part::Extrusion] Extrusion157
  Base = -> Face084
  Dir = (3.5186e-12,2,-2.48463e-10)
  DirMode = 0
  FaceMakerClass = Part::FaceMakerBullseye
  LengthFwd = 0
  LengthRev = 0
  Solid = true
  Symmetric = false
FEATURE [Part::MultiFuse] Fusion001002003002002003011002006002002024003002002
  Shapes = -> [Extrusion156,Extrusion157,Extrusion150,Extrusion154,Extrusion151]
FEATURE [Part::MultiFuse] Fusion001002003002002003011002006002002024003002003
  Shapes = -> [Fusion001002003002002003011002006002002024003002002,Extrusion155]
FEATURE [Part::MultiFuse] Fusion001002003002002003011002006002002024003002004
  Shapes = -> [Fusion001002003002002003011002006002002024003002003,Extrusion153]
FEATURE [Part::Feature] Fusion001002003002002003011002006002002024003002004001  label="Fusion001002003002002003011002006002002024003002005"
  shape: bbox 73.6 x 6 x 14 mm, 20 faces, 3 solids (baked)
FEATURE [Part::MultiFuse] Fusion001002003002002003011002006002002024003002004002
  Shapes = -> [Fusion001002003002002003011002006002002024003002004001,Extrusion146]
FEATURE [Part::MultiFuse] Fusion001002003002002003011002006002002024003002004003
  Shapes = -> [Fusion001002003002002003011002006002002024003002004002,Extrusion147]
FEATURE [Part::Feature] Face086
  shape: bbox 76.5 x 2 x 5.187e-05 mm, 1 faces, 0 solids (baked)
FEATURE [Part::Extrusion] Extrusion159
  Base = -> Face086
  Dir = (-3.04951e-10,-1.58866e-09,-14.4841)
  DirMode = 0
  FaceMakerClass = Part::FaceMakerBullseye
  LengthFwd = 0
  LengthRev = 0
  Solid = true
  Symmetric = false
FEATURE [Part::Part2DObjectPython] Rectangle074  # Draft 2D object (typed FeaturePython)
  ChamferSize = 0
  Columns = 1
  FilletRadius = 0
  Height = 153.926
  Length = 80.7177
  MakeFace = true
  Placement = pos=(-40.7074,-428.522,-245.643) rot=(0.57735,0.57735,0.57735;2.0944rad)
  Rows = 1
  Support = -> [Cut279012005005031002016006009]
FEATURE [Part::FeaturePython] Slice008  # WARN: FeaturePython — macro-defined, semantics opaque (R4)
  Base = -> Cut279012005005031002016006009
  Mode = 1
  Tolerance = 0
  Tools = -> [Rectangle074]
FEATURE [Part::FeaturePython] Slice008_child0  label="Slice008.0"  # WARN: FeaturePython — macro-defined, semantics opaque (R4)
  Base = -> Slice008
  FilterType = 1
  Invert = false
  OverrideMaxVal = 0
  WindowFrom = 80
  WindowTo = 100
  items = 0
FEATURE [Part::FeaturePython] Slice008_child1  label="Slice008.1"  # WARN: FeaturePython — macro-defined, semantics opaque (R4)
  Base = -> Slice008
  FilterType = 1
  Invert = false
  OverrideMaxVal = 0
  Placement = pos=(-1,-5.4854e-11,-3.50838e-10) rot=(0,0,1;0rad)
  WindowFrom = 80
  WindowTo = 100
  items = 1
FEATURE [Part::Feature] Face093
  shape: bbox 3.01e-07 x 6 x 26 mm, 1 faces, 0 solids (baked)
FEATURE [Part::Extrusion] Extrusion164
  Base = -> Face093
  Dir = (-1,1.05257e-11,1.05286e-11)
  DirMode = 0
  FaceMakerClass = Part::FaceMakerBullseye
  LengthFwd = 0
  LengthRev = 0
  Solid = true
  Symmetric = false
FEATURE [Part::MultiFuse] Fusion001002003002002003011002006002002024003002004003006002
  Shapes = -> [Slice008_child0,Extrusion164,Slice008_child1]
FEATURE [App::DocumentObjectGroup] GrExplode_Slice008  label="Exploded Slice009"
  Group = -> [Fusion001002003002002003011002006002002024003002004003006002]
FEATURE [Part::Part2DObjectPython] Circle024  # Draft 2D object (typed FeaturePython)
  FirstAngle = 0
  LastAngle = 0
  MakeFace = true
  Placement = pos=(-2.67276,-275.157,-170.5) rot=(1,0,0;1.5708rad)
  Radius = 2
FEATURE [Part::Part2DObjectPython] Circle025  # Draft 2D object (typed FeaturePython)
  FirstAngle = 0
  LastAngle = 0
  MakeFace = true
  Placement = pos=(-1.24196,-275.157,-170.5) rot=(1,0,0;1.5708rad)
  Radius = 2
FEATURE [Part::Part2DObjectPython] Rectangle083  # Draft 2D object (typed FeaturePython)
  ChamferSize = 0
  Columns = 1
  FilletRadius = 0
  Height = 4.00091
  Length = 1.4308
  MakeFace = true
  Placement = pos=(-2.67276,-275.157,-172.5) rot=(1,0,0;1.5708rad)
  Rows = 1
FEATURE [Part::Extrusion] Extrusion152015
  Base = -> Circle024
  Dir = (2.91638e-11,-3,2.81238e-10)
  DirMode = 0
  FaceMakerClass = Part::FaceMakerBullseye
  LengthFwd = 0
  LengthRev = 0
  Solid = true
  Symmetric = false
FEATURE [Part::Extrusion] Extrusion152016
  Base = -> Rectangle083
  Dir = (2.91638e-11,-3,2.81238e-10)
  DirMode = 0
  FaceMakerClass = Part::FaceMakerBullseye
  LengthFwd = 0
  LengthRev = 0
  Solid = true
  Symmetric = false
FEATURE [Part::Extrusion] Extrusion152017
  Base = -> Circle025
  Dir = (2.91638e-11,-3,2.81238e-10)
  DirMode = 0
  FaceMakerClass = Part::FaceMakerBullseye
  LengthFwd = 0
  LengthRev = 0
  Solid = true
  Symmetric = false
FEATURE [Part::MultiFuse] Fusion001002003002002003011002006002002024003002004003006007
  Shapes = -> [Extrusion152015,Extrusion152017,Extrusion152016]
FEATURE [Part::Part2DObjectPython] Circle026  # Draft 2D object (typed FeaturePython)
  FirstAngle = 0
  LastAngle = 0
  MakeFace = true
  Placement = pos=(-2.67276,-278.157,-170.5) rot=(1,0,0;1.5708rad)
  Radius = 4
  Support = -> [Fusion001002003002002003011002006002002024003002004003006007]
FEATURE [Part::Part2DObjectPython] Circle027  # Draft 2D object (typed FeaturePython)
  FirstAngle = 0
  LastAngle = 0
  MakeFace = true
  Placement = pos=(-1.24196,-278.157,-170.5) rot=(1,0,0;1.5708rad)
  Radius = 4
  Support = -> [Circle026]
FEATURE [Part::Part2DObjectPython] Rectangle084  # Draft 2D object (typed FeaturePython)
  ChamferSize = 0
  Columns = 1
  FilletRadius = 0
  Height = 8.00024
  Length = 1.4308
  MakeFace = true
  Placement = pos=(-2.67276,-278.157,-174.5) rot=(1,0,0;1.5708rad)
  Rows = 1
FEATURE [Part::Extrusion] Extrusion152018
  Base = -> Circle027
  Dir = (-2.91637e-11,3,-2.81238e-10)
  DirMode = 0
  FaceMakerClass = Part::FaceMakerBullseye
  LengthFwd = 0
  LengthRev = 0
  Solid = true
  Symmetric = false
FEATURE [Part::Extrusion] Extrusion152019
  Base = -> Circle026
  Dir = (-2.91637e-11,3,-2.81238e-10)
  DirMode = 0
  FaceMakerClass = Part::FaceMakerBullseye
  LengthFwd = 0
  LengthRev = 0
  Solid = true
  Symmetric = false
FEATURE [Part::Extrusion] Extrusion152020
  Base = -> Rectangle084
  Dir = (-2.91637e-11,3,-2.81238e-10)
  DirMode = 0
  FaceMakerClass = Part::FaceMakerBullseye
  LengthFwd = 0
  LengthRev = 0
  Solid = true
  Symmetric = false
FEATURE [Part::MultiFuse] Fusion001002003002002003011002006002002024003002004003006008
  Shapes = -> [Extrusion152018,Extrusion152019,Extrusion152020]
FEATURE [Part::Part2DObjectPython] Rectangle085  # Draft 2D object (typed FeaturePython)
  ChamferSize = 0
  Columns = 1
  FilletRadius = 0
  Height = 4.00024
  Length = 9.4308
  MakeFace = true
  Placement = pos=(-6.67276,-278.157,-174.5) rot=(1,0,0;1.5708rad)
  Rows = 1
FEATURE [Part::Extrusion] Extrusion152021
  Base = -> Rectangle085
  Dir = (-2.91637e-11,3,-2.81238e-10)
  DirMode = 0
  FaceMakerClass = Part::FaceMakerBullseye
  LengthFwd = 0
  LengthRev = 0
  Solid = true
  Symmetric = false
FEATURE [Part::MultiFuse] Fusion001002003002002003011002006002002024003002004003006009
  Shapes = -> [Fusion001002003002002003011002006002002024003002004003006008,Extrusion152021]
FEATURE [Part::Cut] Cut279012005005031002016006025
  Base = -> Fusion001002003002002003011002006002002024003002004003006009
  Tool = -> Fusion001002003002002003011002006002002024003002004003006007
FEATURE [Part::Part2DObjectPython] Rectangle086  # Draft 2D object (typed FeaturePython)
  ChamferSize = 0
  Columns = 1
  FilletRadius = 0
  Height = 9.4308
  Length = 3
  MakeFace = true
  Placement = pos=(-6.67276,-278.157,-174.5) rot=(0.707107,0.707107,0;3.14159rad)
  Rows = 1
  Support = -> [Cut279012005005031002016006025]
FEATURE [Part::Extrusion] Extrusion152022
  Base = -> Rectangle086
  Dir = (9e-16,9.36821e-11,0.999327)
  DirMode = 0
  FaceMakerClass = Part::FaceMakerBullseye
  LengthFwd = 0
  LengthRev = 0
  Solid = true
  Symmetric = false
FEATURE [Part::Cut] Cut279012005005031002016006026
  Base = -> Cut279012005005031002016006025
  Tool = -> Extrusion152022
FEATURE [Part::Feature] Cut279012005005031002016006026001  label="Cut279012005005031002016006027"
  shape: bbox 9.431 x 3 x 7.001 mm, 15 faces (baked)
FEATURE [Part::Part2DObjectPython] Rectangle087  # Draft 2D object (typed FeaturePython)
  ChamferSize = 0
  Columns = 1
  FilletRadius = 0
  Height = 37.8345
  Length = 21.2901
  MakeFace = true
  Placement = pos=(-6.67276,-312.991,-170.5) rot=(0,0,1;0rad)
  Rows = 1
FEATURE [Part::FeaturePython] Slice009  # WARN: FeaturePython — macro-defined, semantics opaque (R4)
  Base = -> Cut279012005005031002016006026001
  Mode = 1
  Tolerance = 0
  Tools = -> [Rectangle087]
FEATURE [Part::FeaturePython] Slice009_child0  label="Slice009.0"  # WARN: FeaturePython — macro-defined, semantics opaque (R4)
  Base = -> Slice009
  FilterType = 1
  Invert = false
  OverrideMaxVal = 0
  WindowFrom = 80
  WindowTo = 100
  items = 0
FEATURE [Part::FeaturePython] Slice009_child1  label="Slice009.1"  # WARN: FeaturePython — macro-defined, semantics opaque (R4)
  Base = -> Slice009
  FilterType = 1
  Invert = false
  OverrideMaxVal = 0
  WindowFrom = 80
  WindowTo = 100
  items = 1
FEATURE [Part::Feature] Face096
  shape: bbox 9.431 x 3.125e-07 x 3.001 mm, 1 faces, 0 solids (baked)
FEATURE [Part::Extrusion] Extrusion152023
  Base = -> Face096
  Dir = (3.88945e-11,-4,3.74993e-10)
  DirMode = 0
  FaceMakerClass = Part::FaceMakerBullseye
  LengthFwd = 0
  LengthRev = 0
  Solid = true
  Symmetric = false
FEATURE [Part::MultiFuse] Fusion001002003002002003011002006002002024003002004003006010
  Shapes = -> [Extrusion152023,Slice009_child0]
FEATURE [Part::Feature] Face097
  shape: bbox 9.431 x 3.126e-07 x 4 mm, 1 faces, 0 solids (baked)
FEATURE [Part::Extrusion] Extrusion152024
  Base = -> Face097
  Dir = (3.88945e-11,-4,3.74993e-10)
  DirMode = 0
  FaceMakerClass = Part::FaceMakerBullseye
  LengthFwd = 0
  LengthRev = 0
  Solid = true
  Symmetric = false
FEATURE [Part::MultiFuse] Fusion001002003002002003011002006002002024003002004003006011
  Shapes = -> [Slice009_child1,Extrusion152024]
FEATURE [App::DocumentObjectGroup] GrExplode_Slice009  label="Exploded Slice010"
  Group = -> [Fusion001002003002002003011002006002002024003002004003006010,Fusion001002003002002003011002006002002024003002004003006011]
FEATURE [Part::Cone] Cone004
  Angle = 360
  AttacherType = Attacher::AttachEngine3D
  Height = 1.5
  Placement = pos=(39.6156,-284.226,-174.501) rot=(0,0,1;0rad)
  Radius1 = 3
  Radius2 = 1.7
FEATURE [Part::Feature] Fusion001002003002002003011002006002002024003002004003006011003003002002002002005001002001  label="Fusion001002003002002003011002006002002024003002004003006011003003002002002002005001003"
  shape: bbox 22.5 x 9 x 4 mm, 33 faces (baked)
FEATURE [Part::Feature] Cut279012005005031002016006026010003002  label="Cut279012005005031002016006026010005"
  Placement = pos=(-9.46868,-350.336,-26.6995) rot=(0,0,1;0rad)
  shape: bbox 10.9 x 10.3 x 4.3 mm, 10 faces (baked)
FEATURE [Part::Feature] Cut279012005005031002016006026010003003  label="Cut279012005005031002016006026010006"
  Placement = pos=(-9.46868,-335.602,-26.6995) rot=(0,0,1;0rad)
  shape: bbox 10.9 x 10.3 x 4.3 mm, 10 faces (baked)
FEATURE [Part::Extrusion] Extrusion152050002003013
  Dir = (0,0,-2.7)
  DirMode = 0
  FaceMakerClass = Part::FaceMakerBullseye
  LengthFwd = 0
  LengthRev = 0
  Placement = pos=(-138.772,-49.3483,-2.3) rot=(0,0,1;0.523599rad)
  Solid = true
  Symmetric = false
FEATURE [Part::Feature] Cut279012005005031002016006026010003016002  label="Cut279012005005031002016006026010003018"
  Placement = pos=(79.9741,-348.448,-15.9997) rot=(0,0,1;0rad)
  shape: bbox 50.9 x 13.8 x 7 mm, 30 faces (baked)
FEATURE [Part::MultiFuse] Fusion001002003002002003011002006002002024003002004003006011003003002002002002005001002010
  Placement = pos=(0,-107.355,3.18323e-11) rot=(0,0,1;0rad)
FEATURE [Part::MultiFuse] Fusion001002003002002003011002006002002024003002004003006011003003002002002002005001002005
  Placement = pos=(-32.9323,47.7361,2) rot=(0,0,1;0rad)
  Shapes = -> [Extrusion076]
FEATURE [Part::MultiFuse] Fusion001002003002002003011002006002002024003002004003006011003003002002002002005001002008
  Placement = pos=(0,-107.355,3.18323e-11) rot=(0,0,1;0rad)
FEATURE [Part::Feature] Fusion001002003002002003011002006002002025004001  label="Fusion001002003002002003011002006002002025005"
  Placement = pos=(25.6924,-309.741,-14.9997) rot=(0,0,1;1.5708rad)
  shape: bbox 25.5 x 53 x 14 mm, 30 faces (baked)
FEATURE [Part::Cut] Cut002016
  Base = -> Fusion001002003002002003011002006002002024003002004003006011003003002002002002005001002001
  Placement = pos=(9.28133,-91.148,1.02797e-08) rot=(0,0,1;0rad)
  Tool = -> Extrusion060
FEATURE [Part::Cut] Cut279012005005031002016006026010003016003
  Base = -> Fusion001002003002002003011002006002002024003002004003006011003003002002002002005001002001
  Tool = -> Extrusion060
FEATURE [Part::MultiFuse] Fusion001002003002002003011002006002002024003002004003006011003003002002002002005001002011
  Shapes = -> [Fusion001002003002002003011002006002002024003002004003006011003003002002002002005001002010,Fusion001002003002002003011002006002002024003002004003006011003003002002002002005001002008,Fusion001002003002002003011002006002002025004001,Fusion001002003002002003011002006002002024003002004003006011003003002002002002005001002005]
FEATURE [Part::Part2DObjectPython] Circle028  # Draft 2D object (typed FeaturePython)
  FirstAngle = 0
  LastAngle = 0
  MakeFace = true
  Placement = pos=(25.2926,-236.512,-149.001) rot=(0.57735,0.57735,0.57735;2.0944rad)
  Radius = 1.7
FEATURE [Part::Extrusion] Extrusion152050002003014
  Base = -> Circle028
  Dir = (-7.5,0,0)
  DirMode = 0
  FaceMakerClass = Part::FaceMakerBullseye
  LengthFwd = 0
  LengthRev = 0
  Solid = true
  Symmetric = false
FEATURE [Part::MultiFuse] Fusion001002003002002003011002006002002024003002004003006011003003002002002002005001002012
  Shapes = -> [Fusion001002003002002003011002006002002024003002004003006011003003002002002002005001002011,Extrusion152050002003014]
FEATURE [Part::Part2DObjectPython] Circle029  # Draft 2D object (typed FeaturePython)
  FirstAngle = 0
  LastAngle = 0
  MakeFace = true
  Placement = pos=(25.2926,-236.512,-149.001) rot=(0.57735,0.57735,0.57735;2.0944rad)
  Radius = 1.5
  Support = -> [Fusion001002003002002003011002006002002024003002004003006011003003002002002002005001002012]
FEATURE [Part::Extrusion] Extrusion152050002003015
  Base = -> Circle029
  Dir = (-42.0018,0,0)
  DirMode = 0
  FaceMakerClass = Part::FaceMakerBullseye
  LengthFwd = 0
  LengthRev = 0
  Solid = true
  Symmetric = false
FEATURE [Part::Cut] Cut279012005005031002016006026010003016004
  Base = -> Fusion001002003002002003011002006002002024003002004003006011003003002002002002005001002012
  Tool = -> Extrusion152050002003015
FEATURE [Part::Part2DObjectPython] Circle030  # Draft 2D object (typed FeaturePython)
  FirstAngle = 0
  LastAngle = 0
  MakeFace = true
  Placement = pos=(21.5426,-234.012,-123.901) rot=(0,0,1;0rad)
  Radius = 1.56434
  Support = -> [Cut279012005005031002016006026010003016004]
FEATURE [Part::Extrusion] Extrusion152050002003016
  Base = -> Circle030
  Dir = (-4.12658e-10,-2.14981e-09,-19.6)
  DirMode = 0
  FaceMakerClass = Part::FaceMakerBullseye
  LengthFwd = 0
  LengthRev = 0
  Solid = true
  Symmetric = false
FEATURE [Part::MultiFuse] Fusion001002003002002003011002006002002024003002004003006011003003002002002002005001002013
  Shapes = -> [Cut279012005005031002016006026010003016004,Extrusion152050002003016]
FEATURE [Part::Part2DObjectPython] Circle031  # Draft 2D object (typed FeaturePython)
  FirstAngle = 0
  LastAngle = 0
  MakeFace = true
  Placement = pos=(21.4881,-235.96,-123.901) rot=(0,0,1;0rad)
  Radius = 1.5
FEATURE [Part::Extrusion] Extrusion152050002003017
  Base = -> Circle031
  Dir = (-4.2108e-10,-2.19368e-09,-20)
  DirMode = 0
  FaceMakerClass = Part::FaceMakerBullseye
  LengthFwd = 0
  LengthRev = 0
  Solid = true
  Symmetric = false
FEATURE [Part::Cut] Cut279012005005031002016006026010003016005
  Base = -> Fusion001002003002002003011002006002002024003002004003006011003003002002002002005001002013
  Tool = -> Extrusion152050002003017
FEATURE [Part::Feature] Slice006_child1001  label="Slice006.002"
  Placement = pos=(-59.8265,-335.318,-14.9997) rot=(0,0,1;3.14159rad)
  shape: bbox 24.4 x 17.9 x 14 mm, 18 faces (baked)
FEATURE [Part::MultiFuse] Fusion001002003002002003011002006002002024003002004003006011003003002002002002005001002014
  Shapes = -> [Cut279012005005031002016006026010003016005,Slice006_child1001]
FEATURE [Part::Feature] Face099
  Placement = pos=(-5.28864,-159.655,1.13424e-07) rot=(0,0,1;0rad)
  shape: bbox 2.861 x 9.444e-05 x 10.66 mm, 1 faces, 0 solids (baked)
FEATURE [Part::Extrusion] Extrusion152050002003018
  Base = -> Face099
  Dir = (-3.658e-12,-0.5,4.04715e-10)
  DirMode = 0
  FaceMakerClass = Part::FaceMakerBullseye
  LengthFwd = 0
  LengthRev = 0
  Solid = true
  Symmetric = false
FEATURE [Part::MultiFuse] Fusion001002003002002003011002006002002024003002004003006011003003002002002002005001002015
  Shapes = -> [Extrusion152050002003018,Fusion001002003002002003011002006002002024003002004003006011003003002002002002005001002014]
FEATURE [Part::Feature] Face100
  Placement = pos=(0,-107.355,3.18323e-11) rot=(0,0,1;0rad)
  shape: bbox 2.3 x 9.433e-05 x 10.66 mm, 1 faces, 0 solids (baked)
FEATURE [Part::Extrusion] Extrusion152050002003019
  Base = -> Face100
  Dir = (-3.674e-12,-0.5,4.04715e-10)
  DirMode = 0
  FaceMakerClass = Part::FaceMakerBullseye
  LengthFwd = 0
  LengthRev = 0
  Solid = true
  Symmetric = false
FEATURE [Part::MultiFuse] Fusion001002003002002003011002006002002024003002004003006011003003002002002002005001002016
  Shapes = -> [Extrusion152050002003019,Fusion001002003002002003011002006002002024003002004003006011003003002002002002005001002015]
FEATURE [Part::MultiFuse] Fusion001002003002002003011002006002002024003002004003006011003003002002002002005001002017
  Shapes = -> [Extrusion152050002003019,Fusion001002003002002003011002006002002024003002004003006011003003002002002002005001002015]
FEATURE [Part::Feature] Fusion001002003002002003011002006002002025004002004003002001  label="Fusion001002003002002003011002006002002025004002004003003"
  Placement = pos=(52.2924,-319.141,-14.9997) rot=(0,0,1;1.5708rad)
  shape: bbox 14.6 x 28.8 x 14 mm, 256 faces (baked)
FEATURE [Part::Part2DObjectPython] Rectangle088  # Draft 2D object (typed FeaturePython)
  ChamferSize = 0
  Columns = 1
  FilletRadius = 0
  Height = 28.8
  Length = 11.3664
  MakeFace = true
  Placement = pos=(13.9263,-277.012,-158.501) rot=(0,0,1;0rad)
  Rows = 1
  Support = -> [Fusion001002003002002003011002006002002024003002004003006011003003002002002002005001002017]
FEATURE [Part::Extrusion] Extrusion152050002003020
  Base = -> Rectangle088
  Dir = (-1.50942e-10,-9.52777e-11,-13.9997)
  DirMode = 0
  FaceMakerClass = Part::FaceMakerBullseye
  LengthFwd = 0
  LengthRev = 0
  Solid = true
  Symmetric = false
FEATURE [Part::Cut] Cut279012005005031002016006026010003016006
  Base = -> Fusion001002003002002003011002006002002024003002004003006011003003002002002002005001002017
  Tool = -> Extrusion152050002003020
FEATURE [Part::Part2DObjectPython] Rectangle089  # Draft 2D object (typed FeaturePython)
  ChamferSize = 0
  Columns = 1
  FilletRadius = 0
  Height = 95.5141
  Length = 89.2226
  MakeFace = true
  Placement = pos=(25.2926,-294.691,-104.81) rot=(-0.57735,-0.57735,0.57735;2.0944rad)
  Rows = 1
  Support = -> [Cut279012005005031002016006026010003016006]
FEATURE [Part::FeaturePython] Slice010  # WARN: FeaturePython — macro-defined, semantics opaque (R4)
  Base = -> Fusion001002003002002003011002006002002025004002004003002001
  Mode = 1
  Tolerance = 0
  Tools = -> [Rectangle089]
FEATURE [Part::FeaturePython] Slice010_child0  label="Slice010.0"  # WARN: FeaturePython — macro-defined, semantics opaque (R4)
  Base = -> Slice010
  FilterType = 1
  Invert = false
  OverrideMaxVal = 0
  WindowFrom = 80
  WindowTo = 100
  items = 0
FEATURE [Part::FeaturePython] Slice010_child1  label="Slice010.1"  # WARN: FeaturePython — macro-defined, semantics opaque (R4)
  Base = -> Slice010
  FilterType = 1
  Invert = false
  OverrideMaxVal = 0
  WindowFrom = 80
  WindowTo = 100
  items = 1
FEATURE [Part::Feature] Face101
  shape: bbox 2.048e-05 x 10.4 x 2 mm, 1 faces, 0 solids (baked)
FEATURE [Part::Extrusion] Extrusion152050002003021
  Base = -> Face101
  Dir = (-0.233643,0,1.3688e-12)
  DirMode = 0
  FaceMakerClass = Part::FaceMakerBullseye
  LengthFwd = 0
  LengthRev = 0
  Solid = true
  Symmetric = false
FEATURE [Part::Feature] Face102
  shape: bbox 2.048e-05 x 10.4 x 2 mm, 1 faces, 0 solids (baked)
FEATURE [Part::Extrusion] Extrusion152050002003022
  Base = -> Face102
  Dir = (-0.233643,0,1.3688e-12)
  DirMode = 0
  FaceMakerClass = Part::FaceMakerBullseye
  LengthFwd = 0
  LengthRev = 0
  Solid = true
  Symmetric = false
FEATURE [Part::Feature] Face103
  shape: bbox 2.048e-05 x 10.4 x 2 mm, 1 faces, 0 solids (baked)
FEATURE [Part::Extrusion] Extrusion152050002003023
  Base = -> Face103
  Dir = (-0.233643,0,1.3688e-12)
  DirMode = 0
  FaceMakerClass = Part::FaceMakerBullseye
  LengthFwd = 0
  LengthRev = 0
  Solid = true
  Symmetric = false
FEATURE [Part::Feature] Face104
  shape: bbox 2.048e-05 x 10.4 x 2 mm, 1 faces, 0 solids (baked)
FEATURE [Part::Extrusion] Extrusion152050002003024
  Base = -> Face104
  Dir = (-0.233643,0,1.3688e-12)
  DirMode = 0
  FaceMakerClass = Part::FaceMakerBullseye
  LengthFwd = 0
  LengthRev = 0
  Solid = true
  Symmetric = false
FEATURE [Part::Cut] Cut279012005005031002016006026010003016007
  Base = -> Cut279012005005031002016006026010003016006
  Tool = -> Extrusion152050002003024
FEATURE [Part::Cut] Cut279012005005031002016006026010003016008
  Base = -> Cut279012005005031002016006026010003016007
  Tool = -> Extrusion152050002003023
FEATURE [Part::MultiFuse] Fusion001002003002002003011002006002002024003002004003006011003003002002002002005001002018
  Shapes = -> [Extrusion152050002003022,Extrusion152050002003021,Cut279012005005031002016006026010003016008]
FEATURE [Part::Feature] Face106
  Placement = pos=(52.2924,-319.141,-14.9997) rot=(0,0,1;1.5708rad)
  shape: bbox 2 x 8.4 x 2.047e-05 mm, 1 faces, 0 solids (baked)
FEATURE [Part::Extrusion] Extrusion152050002003025
  Base = -> Face106
  Dir = (3.5173e-12,4.6548e-12,0.6)
  DirMode = 0
  FaceMakerClass = Part::FaceMakerBullseye
  LengthFwd = 0
  LengthRev = 0
  Solid = true
  Symmetric = false
FEATURE [Part::Feature] Face107
  Placement = pos=(52.2924,-319.141,-14.9997) rot=(0,0,1;1.5708rad)
  shape: bbox 2 x 8.4 x 2.037e-05 mm, 1 faces, 0 solids (baked)
FEATURE [Part::Extrusion] Extrusion152050002003026
  Base = -> Face107
  Dir = (3.5106e-12,4.6548e-12,0.6)
  DirMode = 0
  FaceMakerClass = Part::FaceMakerBullseye
  LengthFwd = 0
  LengthRev = 0
  Solid = true
  Symmetric = false
FEATURE [Part::MultiFuse] Fusion001002003002002003011002006002002024003002004003006011003003002002002002005001002019
  Shapes = -> [Slice010_child1,Extrusion152050002003025,Extrusion152050002003026]
FEATURE [App::DocumentObjectGroup] GrExplode_Slice010  label="Exploded Slice011"
  Group = -> [Slice010_child0,Fusion001002003002002003011002006002002024003002004003006011003003002002002002005001002019]
FEATURE [Part::Feature] Face109
  Placement = pos=(25.6924,-309.741,-14.9997) rot=(0,0,1;1.5708rad)
  shape: bbox 25.5 x 2.047e-05 x 14 mm, 1 faces, 0 solids (baked)
FEATURE [Part::Extrusion] Extrusion152050002003027
  Base = -> Face109
  Dir = (1.9e-15,-1,1.3881e-12)
  DirMode = 0
  FaceMakerClass = Part::FaceMakerBullseye
  LengthFwd = 0
  LengthRev = 0
  Solid = true
  Symmetric = false
FEATURE [Part::MultiFuse] Fusion001002003002002003011002006002002024003002004003006011003003002002002002005001002020
  Shapes = -> [Fusion001002003002002003011002006002002024003002004003006011003003002002002002005001002018,Extrusion152050002003027]
FEATURE [Part::Part2DObjectPython] Circle033  # Draft 2D object (typed FeaturePython)
  FirstAngle = 0
  LastAngle = 0
  MakeFace = true
  Placement = pos=(27.0263,-252.312,-165.609) rot=(0.57735,0.57735,0.57735;2.0944rad)
  Radius = 2.1085
FEATURE [Part::Part2DObjectPython] Rectangle090  # Draft 2D object (typed FeaturePython)
  ChamferSize = 0
  Columns = 1
  FilletRadius = 0
  Height = 4.21698
  Length = 5.2
  MakeFace = true
  Placement = pos=(27.0263,-257.512,-167.718) rot=(0.57735,0.57735,0.57735;2.0944rad)
  Rows = 1
FEATURE [Part::Part2DObjectPython] Circle034  # Draft 2D object (typed FeaturePython)
  FirstAngle = 0
  LastAngle = 0
  MakeFace = true
  Placement = pos=(41.1529,-260.444,-171.801) rot=(0,0,1;0rad)
  Radius = 2.11
  Support = -> [Extrusion152050002003013]
FEATURE [Part::Part2DObjectPython] Circle035  # Draft 2D object (typed FeaturePython)
  FirstAngle = 0
  LastAngle = 0
  MakeFace = true
  Placement = pos=(41.1529,-255.244,-171.801) rot=(0,0,1;0rad)
  Radius = 2.11
FEATURE [Part::Part2DObjectPython] Rectangle091  # Draft 2D object (typed FeaturePython)
  ChamferSize = 0
  Columns = 1
  FilletRadius = 0
  Height = 5.2
  Length = 4.22
  MakeFace = true
  Placement = pos=(39.0429,-260.444,-171.801) rot=(0,0,1;0rad)
  Rows = 1
FEATURE [Part::Extrusion] Extrusion152050002003030
  Base = -> Circle035
  Dir = (0,0,1.73)
  DirMode = 0
  FaceMakerClass = Part::FaceMakerBullseye
  LengthFwd = 0
  LengthRev = 0
  Solid = true
  Symmetric = false
FEATURE [Part::Extrusion] Extrusion152050002003031
  Base = -> Circle034
  Dir = (9e-16,2.14868e-10,1.73)
  DirMode = 0
  FaceMakerClass = Part::FaceMakerBullseye
  LengthFwd = 0
  LengthRev = 0
  Solid = true
  Symmetric = false
FEATURE [Part::Extrusion] Extrusion152050002003032
  Base = -> Rectangle091
  Dir = (9e-16,2.14868e-10,1.73)
  DirMode = 0
  FaceMakerClass = Part::FaceMakerBullseye
  LengthFwd = 0
  LengthRev = 0
  Solid = true
  Symmetric = false
FEATURE [Part::MultiFuse] Fusion001002003002002003011002006002002024003002004003006011003003002002002002005001002021
  Placement = pos=(-132.758,-6.06917e-10,-210.844) rot=(0,-1,0;1.5708rad)
  Shapes = -> [Extrusion152050002003031,Extrusion152050002003032,Extrusion152050002003030]
FEATURE [Part::MultiFuse] Fusion001002003002002003011002006002002024003002004003006011003003002002002002005001002022
  Placement = pos=(-132.758,-6.06917e-10,-210.844) rot=(0,-1,0;1.5708rad)
  Shapes = -> [Extrusion152050002003031,Extrusion152050002003032,Extrusion152050002003030]
FEATURE [Part::Part2DObjectPython] Circle036  # Draft 2D object (typed FeaturePython)
  FirstAngle = 0
  LastAngle = 0
  MakeFace = true
  Placement = pos=(39.0429,-255.244,-169.691) rot=(0.57735,0.57735,0.57735;2.0944rad)
  Radius = 2.4
  Support = -> [Fusion001002003002002003011002006002002024003002004003006011003003002002002002005001002021]
FEATURE [Part::Part2DObjectPython] Circle037  # Draft 2D object (typed FeaturePython)
  FirstAngle = 0
  LastAngle = 0
  MakeFace = true
  Placement = pos=(39.0429,-249.844,-169.691) rot=(0.57735,0.57735,0.57735;2.0944rad)
  Radius = 2.39644
  Support = -> [Circle036]
FEATURE [Part::Part2DObjectPython] Rectangle092  # Draft 2D object (typed FeaturePython)
  ChamferSize = 0
  Columns = 1
  FilletRadius = 0
  Height = 4.79644
  Length = 5.4
  MakeFace = true
  Placement = pos=(39.0429,-255.244,-172.087) rot=(0.57735,0.57735,0.57735;2.0944rad)
  Rows = 1
FEATURE [Part::Extrusion] Extrusion152050002003033
  Base = -> Circle037
  Dir = (-1.73,0,0)
  DirMode = 0
  FaceMakerClass = Part::FaceMakerBullseye
  LengthFwd = 0
  LengthRev = 0
  Solid = true
  Symmetric = false
FEATURE [Part::Extrusion] Extrusion152050002003034
  Base = -> Rectangle092
  Dir = (-1.73,0,0)
  DirMode = 0
  FaceMakerClass = Part::FaceMakerBullseye
  LengthFwd = 0
  LengthRev = 0
  Solid = true
  Symmetric = false
FEATURE [Part::Extrusion] Extrusion152050002003035
  Base = -> Circle036
  Dir = (-1.73,0,0)
  DirMode = 0
  FaceMakerClass = Part::FaceMakerBullseye
  LengthFwd = 0
  LengthRev = 0
  Solid = true
  Symmetric = false
FEATURE [Part::MultiFuse] Fusion001002003002002003011002006002002024003002004003006011003003002002002002005001002023
  Placement = pos=(-12.0166,-2.37568,4.07546) rot=(0,0,1;0rad)
  Shapes = -> [Extrusion152050002003035,Extrusion152050002003034,Extrusion152050002003033]
FEATURE [Part::MultiFuse] Fusion001002003002002003011002006002002024003002004003006011003003002002002002005001002024
  Placement = pos=(-12.0166,-16.7757,4.07546) rot=(0,0,1;0rad)
  Shapes = -> [Extrusion152050002003035,Extrusion152050002003034,Extrusion152050002003033]
FEATURE [Part::MultiFuse] Fusion001002003002002003011002006002002024003002004003006011003003002002002002005001002025
  Shapes = -> [Fusion001002003002002003011002006002002024003002004003006011003003002002002002005001002020,Fusion001002003002002003011002006002002024003002004003006011003003002002002002005001002024,Fusion001002003002002003011002006002002024003002004003006011003003002002002002005001002023]
FEATURE [Part::MultiFuse] Fusion001002003002002003011002006002002024003002004003006011003003002002002002005001002026
  Placement = pos=(-132.758,-6.06917e-10,-210.844) rot=(0,-1,0;1.5708rad)
  Shapes = -> [Extrusion152050002003031,Extrusion152050002003032,Extrusion152050002003030]
FEATURE [Part::Feature] Face111
  Placement = pos=(-132.758,-6.06917e-10,-210.844) rot=(0,-1,0;1.5708rad)
  shape: bbox 2.138e-07 x 5.2 x 4.22 mm, 1 faces, 0 solids (baked)
FEATURE [Part::Extrusion] Extrusion152050002003036
  Base = -> Face111
  Dir = (10.2508,-1.1484e-09,4.46606e-10)
  DirMode = 0
  FaceMakerClass = Part::FaceMakerBullseye
  LengthFwd = 0
  LengthRev = 0
  Solid = true
  Symmetric = false
FEATURE [Part::Feature] Face112
  Placement = pos=(-132.758,-6.06917e-10,-210.844) rot=(0,-1,0;1.5708rad)
  shape: bbox 2.134e-07 x 2.11 x 4.22 mm, 1 faces, 0 solids (baked)
FEATURE [Part::Extrusion] Extrusion152050002003037
  Base = -> Face112
  Dir = (10.2508,-1.1484e-09,4.46606e-10)
  DirMode = 0
  FaceMakerClass = Part::FaceMakerBullseye
  LengthFwd = 0
  LengthRev = 0
  Solid = true
  Symmetric = false
FEATURE [Part::Feature] Face113
  Placement = pos=(-132.758,-6.06917e-10,-210.844) rot=(0,-1,0;1.5708rad)
  shape: bbox 2.134e-07 x 2.11 x 4.22 mm, 1 faces, 0 solids (baked)
FEATURE [Part::Extrusion] Extrusion152050002003038
  Base = -> Face113
  Dir = (10.2508,-1.1484e-09,4.46606e-10)
  DirMode = 0
  FaceMakerClass = Part::FaceMakerBullseye
  LengthFwd = 0
  LengthRev = 0
  Solid = true
  Symmetric = false
FEATURE [Part::Feature] Face114
  Placement = pos=(-132.758,-6.06917e-10,-210.844) rot=(0,-1,0;1.5708rad)
  shape: bbox 2.003e-07 x 2.11 x 4.22 mm, 1 faces, 0 solids (baked)
FEATURE [Part::Extrusion] Extrusion152050002003039
  Base = -> Face114
  Dir = (10.2508,-1.1484e-09,4.46606e-10)
  DirMode = 0
  FaceMakerClass = Part::FaceMakerBullseye
  LengthFwd = 0
  LengthRev = 0
  Solid = true
  Symmetric = false
FEATURE [Part::Feature] Face115
  Placement = pos=(-132.758,-6.06917e-10,-210.844) rot=(0,-1,0;1.5708rad)
  shape: bbox 2.003e-07 x 2.11 x 4.22 mm, 1 faces, 0 solids (baked)
FEATURE [Part::Extrusion] Extrusion152050002003040
  Base = -> Face115
  Dir = (10.2508,-1.1484e-09,4.46615e-10)
  DirMode = 0
  FaceMakerClass = Part::FaceMakerBullseye
  LengthFwd = 0
  LengthRev = 0
  Solid = true
  Symmetric = false
FEATURE [Part::MultiFuse] Fusion001002003002002003011002006002002024003002004003006011003003002002002002005001002027
  Placement = pos=(-22.2674,2.92674,2.77872) rot=(0,0,1;0rad)
  Shapes = -> [Extrusion152050002003040,Extrusion152050002003037,Extrusion152050002003039,Extrusion152050002003038,Extrusion152050002003036]
FEATURE [Part::Cut] Cut279012005005031002016006026010003016009
  Base = -> Fusion001002003002002003011002006002002024003002004003006011003003002002002002005001002025
  Tool = -> Fusion001002003002002003011002006002002024003002004003006011003003002002002002005001002027
FEATURE [Part::Feature] Fusion001002003002002003011002006002002024003002004003006011003003002002002002005001002026001  label="Fusion001002003002002003011002006002002024003002004003006011003003002002002002005001002028"
  shape: bbox 1.73 x 9.42 x 4.22 mm, 6 faces (baked)
FEATURE [Part::Feature] Face116
  shape: bbox 2.141e-07 x 9.42 x 4.22 mm, 1 faces, 0 solids (baked)
FEATURE [Part::Extrusion] Extrusion152050002003041
  Base = -> Face116
  Dir = (12.3569,-1.38425e-09,5.38368e-10)
  DirMode = 0
  FaceMakerClass = Part::FaceMakerBullseye
  LengthFwd = 0
  LengthRev = 0
  Placement = pos=(-24.3735,-11.4733,2.78904) rot=(0,0,1;0rad)
  Solid = true
  Symmetric = false
FEATURE [Part::Cut] Cut279012005005031002016006026010003016010
  Base = -> Cut279012005005031002016006026010003016009
  Tool = -> Extrusion152050002003041
note: 6 file-system paths scrubbed to <path> (originals preserved in the JSON sidecar)
